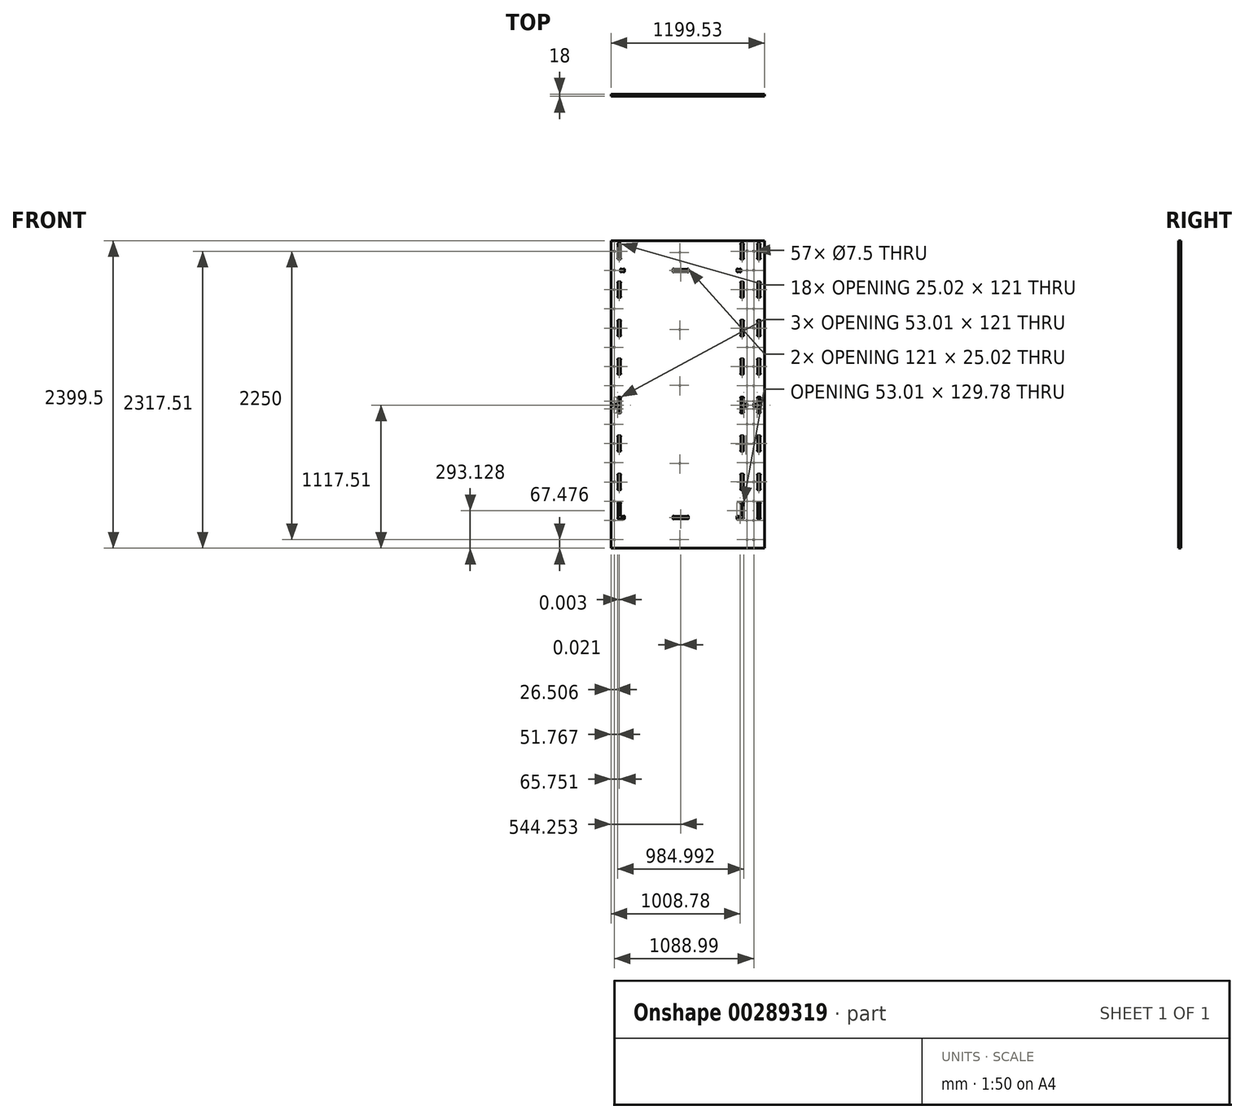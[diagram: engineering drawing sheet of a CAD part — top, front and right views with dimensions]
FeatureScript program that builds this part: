
annotation { "Feature Type Name" : "Feature", "Feature Type Description" : "" }
export const myFeature = defineFeature(function(context is Context, id is Id, definition is map)
    precondition{}
    {
        {
            var Q0;
            Q0=qCreatedBy(makeId("Front.planeOp"),FACE);
            var sketch = newSketch(context, id + "F0", { "sketchPlane" : qUnion([Q0])});
            skLineSegment(sketch, "E0", {"start": v(-600, -1200) * mm, "end": v(600, -1200) * mm});
            skLineSegment(sketch, "E1", {"start": v(600, -1200) * mm, "end": v(600, 1200) * mm});
            skLineSegment(sketch, "E2", {"start": v(600, 1200) * mm, "end": v(-600, 1200) * mm});
            skLineSegment(sketch, "E3", {"start": v(-600, 1200) * mm, "end": v(-600, -1200) * mm});
            skLineSegment(sketch, "E4", {"start": v(599.53, -1200) * mm, "end": v(599.5, 1199.5) * mm});
            skLineSegment(sketch, "E5", {"start": v(599.5, 1199.5) * mm, "end": v(-600, 1199.5) * mm});
            skArc(sketch, "E6", {"start": v(-543.49, 278) * mm, "mid": v(-546.75, 274.87) * mm, "end": v(-543.74, 271.5) * mm});
            skLineSegment(sketch, "E7", {"start": v(-543.74, 271.5) * mm, "end": v(-543.74, 163.52) * mm});
            skArc(sketch, "E8", {"start": v(-543.74, 163.52) * mm, "mid": v(-546.75, 160.14) * mm, "end": v(-543.49, 157) * mm});
            skLineSegment(sketch, "E9", {"start": v(-543.49, 157) * mm, "end": v(-524.99, 157) * mm});
            skArc(sketch, "E10", {"start": v(-524.99, 157) * mm, "mid": v(-521.73, 160.14) * mm, "end": v(-524.74, 163.52) * mm});
            skLineSegment(sketch, "E11", {"start": v(-524.74, 163.52) * mm, "end": v(-524.74, 271.5) * mm});
            skArc(sketch, "E12", {"start": v(-524.74, 271.5) * mm, "mid": v(-521.73, 274.87) * mm, "end": v(-524.99, 278) * mm});
            skLineSegment(sketch, "E13", {"start": v(-524.99, 278) * mm, "end": v(-543.49, 278) * mm});
            skArc(sketch, "E14", {"start": v(-524.74, -28.5) * mm, "mid": v(-521.73, -25.13) * mm, "end": v(-524.99, -22) * mm});
            skLineSegment(sketch, "E15", {"start": v(-524.99, -22) * mm, "end": v(-543.49, -22) * mm});
            skArc(sketch, "E16", {"start": v(-543.49, -22) * mm, "mid": v(-546.75, -25.13) * mm, "end": v(-543.74, -28.5) * mm});
            skLineSegment(sketch, "E17", {"start": v(-543.74, -28.5) * mm, "end": v(-543.74, -73) * mm});
            skLineSegment(sketch, "E18", {"start": v(-543.74, -73) * mm, "end": v(-568.23, -73) * mm});
            skArc(sketch, "E19", {"start": v(-568.23, -73) * mm, "mid": v(-571.6, -69.99) * mm, "end": v(-574.74, -73.25) * mm});
            skLineSegment(sketch, "E20", {"start": v(-574.74, -73.25) * mm, "end": v(-574.74, -91.75) * mm});
            skArc(sketch, "E21", {"start": v(-574.74, -91.75) * mm, "mid": v(-571.6, -95) * mm, "end": v(-568.23, -92) * mm});
            skLineSegment(sketch, "E22", {"start": v(-568.23, -92) * mm, "end": v(-543.74, -92) * mm});
            skLineSegment(sketch, "E23", {"start": v(-543.74, -92) * mm, "end": v(-543.74, -136.48) * mm});
            skArc(sketch, "E24", {"start": v(-543.74, -136.48) * mm, "mid": v(-546.74, -139.86) * mm, "end": v(-543.49, -143) * mm});
            skLineSegment(sketch, "E25", {"start": v(-543.49, -143) * mm, "end": v(-524.99, -143) * mm});
            skArc(sketch, "E26", {"start": v(-524.99, -143) * mm, "mid": v(-521.73, -139.86) * mm, "end": v(-524.74, -136.48) * mm});
            skLineSegment(sketch, "E27", {"start": v(-524.74, -136.48) * mm, "end": v(-524.74, -28.5) * mm});
            skArc(sketch, "E28", {"start": v(-524.73, -328.5) * mm, "mid": v(-521.73, -325.13) * mm, "end": v(-524.98, -322) * mm});
            skLineSegment(sketch, "E29", {"start": v(-524.98, -322) * mm, "end": v(-543.48, -322) * mm});
            skArc(sketch, "E30", {"start": v(-543.48, -322) * mm, "mid": v(-546.74, -325.13) * mm, "end": v(-543.73, -328.5) * mm});
            skLineSegment(sketch, "E31", {"start": v(-543.73, -328.5) * mm, "end": v(-543.73, -436.48) * mm});
            skArc(sketch, "E32", {"start": v(-543.73, -436.48) * mm, "mid": v(-546.74, -439.86) * mm, "end": v(-543.48, -443) * mm});
            skLineSegment(sketch, "E33", {"start": v(-543.48, -443) * mm, "end": v(-524.98, -443) * mm});
            skArc(sketch, "E34", {"start": v(-524.98, -443) * mm, "mid": v(-521.72, -439.86) * mm, "end": v(-524.73, -436.48) * mm});
            skLineSegment(sketch, "E35", {"start": v(-524.73, -436.48) * mm, "end": v(-524.73, -328.5) * mm});
            skArc(sketch, "E36", {"start": v(-524.73, -628.5) * mm, "mid": v(-521.72, -625.13) * mm, "end": v(-524.98, -622) * mm});
            skLineSegment(sketch, "E37", {"start": v(-524.98, -622) * mm, "end": v(-543.48, -622) * mm});
            skArc(sketch, "E38", {"start": v(-543.48, -622) * mm, "mid": v(-546.74, -625.13) * mm, "end": v(-543.73, -628.5) * mm});
            skLineSegment(sketch, "E39", {"start": v(-543.73, -628.5) * mm, "end": v(-543.73, -736.48) * mm});
            skArc(sketch, "E40", {"start": v(-543.73, -736.48) * mm, "mid": v(-546.74, -739.86) * mm, "end": v(-543.48, -743) * mm});
            skLineSegment(sketch, "E41", {"start": v(-543.48, -743) * mm, "end": v(-524.98, -743) * mm});
            skArc(sketch, "E42", {"start": v(-524.98, -743) * mm, "mid": v(-521.72, -739.86) * mm, "end": v(-524.73, -736.48) * mm});
            skLineSegment(sketch, "E43", {"start": v(-524.73, -736.48) * mm, "end": v(-524.73, -628.5) * mm});
            skArc(sketch, "E44", {"start": v(-109.71, -949.76) * mm, "mid": v(-113.1, -946.75) * mm, "end": v(-116.23, -950) * mm});
            skLineSegment(sketch, "E45", {"start": v(-116.23, -950) * mm, "end": v(-116.23, -968.5) * mm});
            skArc(sketch, "E46", {"start": v(-116.23, -968.5) * mm, "mid": v(-113.09, -971.77) * mm, "end": v(-109.71, -968.76) * mm});
            skLineSegment(sketch, "E47", {"start": v(-109.71, -968.76) * mm, "end": v(-1.74, -968.76) * mm});
            skArc(sketch, "E48", {"start": v(-1.74, -968.76) * mm, "mid": v(1.64, -971.76) * mm, "end": v(4.77, -968.5) * mm});
            skLineSegment(sketch, "E49", {"start": v(4.77, -968.5) * mm, "end": v(4.77, -950) * mm});
            skArc(sketch, "E50", {"start": v(4.77, -950) * mm, "mid": v(1.64, -946.75) * mm, "end": v(-1.74, -949.76) * mm});
            skLineSegment(sketch, "E51", {"start": v(-1.74, -949.76) * mm, "end": v(-109.71, -949.76) * mm});
            skArc(sketch, "E52", {"start": v(413.27, -736.47) * mm, "mid": v(410.26, -739.84) * mm, "end": v(413.52, -742.98) * mm});
            skLineSegment(sketch, "E53", {"start": v(413.52, -742.98) * mm, "end": v(432.02, -742.98) * mm});
            skArc(sketch, "E54", {"start": v(432.02, -742.98) * mm, "mid": v(435.28, -739.84) * mm, "end": v(432.27, -736.47) * mm});
            skLineSegment(sketch, "E55", {"start": v(432.27, -736.47) * mm, "end": v(432.27, -628.5) * mm});
            skArc(sketch, "E56", {"start": v(432.27, -628.5) * mm, "mid": v(435.28, -625.11) * mm, "end": v(432.02, -621.98) * mm});
            skLineSegment(sketch, "E57", {"start": v(432.02, -621.98) * mm, "end": v(413.52, -621.98) * mm});
            skArc(sketch, "E58", {"start": v(413.52, -621.98) * mm, "mid": v(410.26, -625.11) * mm, "end": v(413.27, -628.5) * mm});
            skLineSegment(sketch, "E59", {"start": v(413.27, -628.5) * mm, "end": v(413.27, -736.47) * mm});
            skArc(sketch, "E60", {"start": v(432.02, -442.98) * mm, "mid": v(435.28, -439.84) * mm, "end": v(432.27, -436.47) * mm});
            skLineSegment(sketch, "E61", {"start": v(432.27, -436.47) * mm, "end": v(432.27, -328.5) * mm});
            skArc(sketch, "E62", {"start": v(432.27, -328.5) * mm, "mid": v(435.28, -325.11) * mm, "end": v(432.02, -321.98) * mm});
            skLineSegment(sketch, "E63", {"start": v(432.02, -321.98) * mm, "end": v(413.52, -321.98) * mm});
            skArc(sketch, "E64", {"start": v(413.52, -321.98) * mm, "mid": v(410.26, -325.11) * mm, "end": v(413.27, -328.5) * mm});
            skLineSegment(sketch, "E65", {"start": v(413.27, -328.5) * mm, "end": v(413.27, -436.47) * mm});
            skArc(sketch, "E66", {"start": v(413.27, -436.47) * mm, "mid": v(410.26, -439.84) * mm, "end": v(413.52, -442.98) * mm});
            skLineSegment(sketch, "E67", {"start": v(413.52, -442.98) * mm, "end": v(432.02, -442.98) * mm});
            skArc(sketch, "E68", {"start": v(432.01, 157.02) * mm, "mid": v(435.27, 160.16) * mm, "end": v(432.26, 163.53) * mm});
            skLineSegment(sketch, "E69", {"start": v(432.26, 163.53) * mm, "end": v(432.26, 271.51) * mm});
            skArc(sketch, "E70", {"start": v(432.26, 271.51) * mm, "mid": v(435.27, 274.89) * mm, "end": v(432.01, 278.02) * mm});
            skLineSegment(sketch, "E71", {"start": v(432.01, 278.02) * mm, "end": v(413.51, 278.02) * mm});
            skArc(sketch, "E72", {"start": v(413.51, 278.02) * mm, "mid": v(410.25, 274.89) * mm, "end": v(413.26, 271.51) * mm});
            skLineSegment(sketch, "E73", {"start": v(413.26, 271.51) * mm, "end": v(413.26, 163.53) * mm});
            skArc(sketch, "E74", {"start": v(413.26, 163.53) * mm, "mid": v(410.25, 160.16) * mm, "end": v(413.51, 157.02) * mm});
            skLineSegment(sketch, "E75", {"start": v(413.51, 157.02) * mm, "end": v(432.01, 157.02) * mm});
            skArc(sketch, "E76", {"start": v(432, 457.02) * mm, "mid": v(435.27, 460.16) * mm, "end": v(432.26, 463.53) * mm});
            skLineSegment(sketch, "E77", {"start": v(432.26, 463.53) * mm, "end": v(432.26, 571.51) * mm});
            skArc(sketch, "E78", {"start": v(432.26, 571.51) * mm, "mid": v(435.27, 574.89) * mm, "end": v(432, 578.02) * mm});
            skLineSegment(sketch, "E79", {"start": v(432, 578.02) * mm, "end": v(413.5, 578.02) * mm});
            skArc(sketch, "E80", {"start": v(413.5, 578.02) * mm, "mid": v(410.25, 574.89) * mm, "end": v(413.26, 571.51) * mm});
            skLineSegment(sketch, "E81", {"start": v(413.26, 571.51) * mm, "end": v(413.26, 463.53) * mm});
            skArc(sketch, "E82", {"start": v(413.26, 463.53) * mm, "mid": v(410.25, 460.16) * mm, "end": v(413.5, 457.02) * mm});
            skLineSegment(sketch, "E83", {"start": v(413.5, 457.02) * mm, "end": v(432, 457.02) * mm});
            skArc(sketch, "E84", {"start": v(432, 757.02) * mm, "mid": v(435.26, 760.16) * mm, "end": v(432.26, 763.53) * mm});
            skLineSegment(sketch, "E85", {"start": v(432.26, 763.53) * mm, "end": v(432.25, 871.51) * mm});
            skArc(sketch, "E86", {"start": v(432.25, 871.51) * mm, "mid": v(435.26, 874.89) * mm, "end": v(432, 878.02) * mm});
            skLineSegment(sketch, "E87", {"start": v(432, 878.02) * mm, "end": v(413.5, 878.02) * mm});
            skArc(sketch, "E88", {"start": v(413.5, 878.02) * mm, "mid": v(410.25, 874.89) * mm, "end": v(413.25, 871.51) * mm});
            skLineSegment(sketch, "E89", {"start": v(413.25, 871.51) * mm, "end": v(413.26, 763.53) * mm});
            skArc(sketch, "E90", {"start": v(413.26, 763.53) * mm, "mid": v(410.25, 760.16) * mm, "end": v(413.5, 757.02) * mm});
            skLineSegment(sketch, "E91", {"start": v(413.5, 757.02) * mm, "end": v(432, 757.02) * mm});
            skArc(sketch, "E92", {"start": v(545.26, 763.53) * mm, "mid": v(542.25, 760.16) * mm, "end": v(545.5, 757.02) * mm});
            skLineSegment(sketch, "E93", {"start": v(545.5, 757.02) * mm, "end": v(564, 757.02) * mm});
            skArc(sketch, "E94", {"start": v(564, 757.02) * mm, "mid": v(567.26, 760.16) * mm, "end": v(564.26, 763.54) * mm});
            skLineSegment(sketch, "E95", {"start": v(564.26, 763.54) * mm, "end": v(564.25, 871.51) * mm});
            skArc(sketch, "E96", {"start": v(564.25, 871.51) * mm, "mid": v(567.26, 874.89) * mm, "end": v(564, 878.02) * mm});
            skLineSegment(sketch, "E97", {"start": v(564, 878.02) * mm, "end": v(545.5, 878.02) * mm});
            skArc(sketch, "E98", {"start": v(545.5, 878.02) * mm, "mid": v(542.25, 874.89) * mm, "end": v(545.25, 871.51) * mm});
            skLineSegment(sketch, "E99", {"start": v(545.25, 871.51) * mm, "end": v(545.26, 763.53) * mm});
            skArc(sketch, "E100", {"start": v(407.74, 958.01) * mm, "mid": v(411.12, 955) * mm, "end": v(414.25, 958.26) * mm});
            skLineSegment(sketch, "E101", {"start": v(414.25, 958.26) * mm, "end": v(414.25, 976.77) * mm});
            skArc(sketch, "E102", {"start": v(414.25, 976.77) * mm, "mid": v(411.12, 980.03) * mm, "end": v(407.74, 977.02) * mm});
            skLineSegment(sketch, "E103", {"start": v(407.74, 977.02) * mm, "end": v(389.76, 977.02) * mm});
            skArc(sketch, "E104", {"start": v(389.76, 977.02) * mm, "mid": v(386.39, 980.03) * mm, "end": v(383.25, 976.77) * mm});
            skLineSegment(sketch, "E105", {"start": v(383.25, 976.77) * mm, "end": v(383.25, 958.26) * mm});
            skArc(sketch, "E106", {"start": v(383.25, 958.26) * mm, "mid": v(386.39, 955) * mm, "end": v(389.77, 958.01) * mm});
            skLineSegment(sketch, "E107", {"start": v(389.77, 958.01) * mm, "end": v(407.74, 958.01) * mm});
            skArc(sketch, "E108", {"start": v(4.75, 976.76) * mm, "mid": v(1.62, 980.02) * mm, "end": v(-1.76, 977.01) * mm});
            skLineSegment(sketch, "E109", {"start": v(-1.76, 977.01) * mm, "end": v(-109.74, 977.01) * mm});
            skArc(sketch, "E110", {"start": v(-109.74, 977.01) * mm, "mid": v(-113.11, 980.02) * mm, "end": v(-116.25, 976.76) * mm});
            skLineSegment(sketch, "E111", {"start": v(-116.25, 976.76) * mm, "end": v(-116.25, 958.26) * mm});
            skArc(sketch, "E112", {"start": v(-116.25, 958.26) * mm, "mid": v(-113.11, 955) * mm, "end": v(-109.73, 958.01) * mm});
            skLineSegment(sketch, "E113", {"start": v(-109.73, 958.01) * mm, "end": v(-1.76, 958.01) * mm});
            skArc(sketch, "E114", {"start": v(-1.76, 958.01) * mm, "mid": v(1.62, 955) * mm, "end": v(4.75, 958.26) * mm});
            skLineSegment(sketch, "E115", {"start": v(4.75, 958.26) * mm, "end": v(4.75, 976.76) * mm});
            skArc(sketch, "E116", {"start": v(-494.75, 976.76) * mm, "mid": v(-497.88, 980.02) * mm, "end": v(-501.26, 977) * mm});
            skLineSegment(sketch, "E117", {"start": v(-501.26, 977) * mm, "end": v(-519.24, 977) * mm});
            skArc(sketch, "E118", {"start": v(-519.24, 977) * mm, "mid": v(-522.61, 980.02) * mm, "end": v(-525.75, 976.76) * mm});
            skLineSegment(sketch, "E119", {"start": v(-525.75, 976.76) * mm, "end": v(-525.75, 958.26) * mm});
            skArc(sketch, "E120", {"start": v(-525.75, 958.26) * mm, "mid": v(-522.61, 955) * mm, "end": v(-519.24, 958) * mm});
            skLineSegment(sketch, "E121", {"start": v(-519.24, 958) * mm, "end": v(-501.26, 958) * mm});
            skArc(sketch, "E122", {"start": v(-501.26, 958) * mm, "mid": v(-497.88, 955) * mm, "end": v(-494.75, 958.26) * mm});
            skLineSegment(sketch, "E123", {"start": v(-494.75, 958.26) * mm, "end": v(-494.75, 976.76) * mm});
            skArc(sketch, "E124", {"start": v(-543.5, 878) * mm, "mid": v(-546.75, 874.87) * mm, "end": v(-543.75, 871.5) * mm});
            skLineSegment(sketch, "E125", {"start": v(-543.75, 871.5) * mm, "end": v(-543.74, 763.52) * mm});
            skArc(sketch, "E126", {"start": v(-543.74, 763.52) * mm, "mid": v(-546.75, 760.14) * mm, "end": v(-543.5, 757) * mm});
            skLineSegment(sketch, "E127", {"start": v(-543.5, 757) * mm, "end": v(-525, 757) * mm});
            skArc(sketch, "E128", {"start": v(-525, 757) * mm, "mid": v(-521.74, 760.14) * mm, "end": v(-524.75, 763.52) * mm});
            skLineSegment(sketch, "E129", {"start": v(-524.75, 763.52) * mm, "end": v(-524.75, 871.5) * mm});
            skArc(sketch, "E130", {"start": v(-524.75, 871.5) * mm, "mid": v(-521.74, 874.87) * mm, "end": v(-525, 878) * mm});
            skLineSegment(sketch, "E131", {"start": v(-525, 878) * mm, "end": v(-543.5, 878) * mm});
            skArc(sketch, "E132", {"start": v(-524.74, 571.5) * mm, "mid": v(-521.74, 574.87) * mm, "end": v(-525, 578) * mm});
            skLineSegment(sketch, "E133", {"start": v(-525, 578) * mm, "end": v(-543.5, 578) * mm});
            skArc(sketch, "E134", {"start": v(-543.5, 578) * mm, "mid": v(-546.75, 574.87) * mm, "end": v(-543.74, 571.5) * mm});
            skLineSegment(sketch, "E135", {"start": v(-543.74, 571.5) * mm, "end": v(-543.74, 463.52) * mm});
            skArc(sketch, "E136", {"start": v(-543.74, 463.52) * mm, "mid": v(-546.75, 460.14) * mm, "end": v(-543.5, 457) * mm});
            skLineSegment(sketch, "E137", {"start": v(-543.5, 457) * mm, "end": v(-525, 457) * mm});
            skArc(sketch, "E138", {"start": v(-525, 457) * mm, "mid": v(-521.73, 460.14) * mm, "end": v(-524.74, 463.52) * mm});
            skLineSegment(sketch, "E139", {"start": v(-524.74, 463.52) * mm, "end": v(-524.74, 571.5) * mm});
            skArc(sketch, "E140", {"start": v(-525, 1057) * mm, "mid": v(-521.74, 1060.14) * mm, "end": v(-524.75, 1063.52) * mm});
            skLineSegment(sketch, "E141", {"start": v(-524.75, 1063.52) * mm, "end": v(-524.75, 1171.5) * mm});
            skArc(sketch, "E142", {"start": v(-524.75, 1171.5) * mm, "mid": v(-521.74, 1174.87) * mm, "end": v(-525, 1178) * mm});
            skLineSegment(sketch, "E143", {"start": v(-525, 1178) * mm, "end": v(-543.5, 1178) * mm});
            skArc(sketch, "E144", {"start": v(-543.5, 1178) * mm, "mid": v(-546.76, 1174.87) * mm, "end": v(-543.75, 1171.5) * mm});
            skLineSegment(sketch, "E145", {"start": v(-543.75, 1171.5) * mm, "end": v(-543.75, 1063.52) * mm});
            skArc(sketch, "E146", {"start": v(-543.75, 1063.52) * mm, "mid": v(-546.76, 1060.14) * mm, "end": v(-543.5, 1057) * mm});
            skLineSegment(sketch, "E147", {"start": v(-543.5, 1057) * mm, "end": v(-525, 1057) * mm});
            skArc(sketch, "E148", {"start": v(545.25, 1063.54) * mm, "mid": v(542.24, 1060.16) * mm, "end": v(545.5, 1057.02) * mm});
            skLineSegment(sketch, "E149", {"start": v(545.5, 1057.02) * mm, "end": v(564, 1057.02) * mm});
            skArc(sketch, "E150", {"start": v(564, 1057.02) * mm, "mid": v(567.26, 1060.16) * mm, "end": v(564.25, 1063.54) * mm});
            skLineSegment(sketch, "E151", {"start": v(564.25, 1063.54) * mm, "end": v(564.25, 1171.51) * mm});
            skArc(sketch, "E152", {"start": v(564.25, 1171.51) * mm, "mid": v(567.26, 1174.89) * mm, "end": v(564, 1178.02) * mm});
            skLineSegment(sketch, "E153", {"start": v(564, 1178.02) * mm, "end": v(545.5, 1178.02) * mm});
            skArc(sketch, "E154", {"start": v(545.5, 1178.02) * mm, "mid": v(542.24, 1174.89) * mm, "end": v(545.25, 1171.51) * mm});
            skLineSegment(sketch, "E155", {"start": v(545.25, 1171.51) * mm, "end": v(545.25, 1063.54) * mm});
            skLineSegment(sketch, "E156", {"start": v(432.25, 1063.53) * mm, "end": v(432.25, 1171.51) * mm});
            skArc(sketch, "E157", {"start": v(432.25, 1171.51) * mm, "mid": v(435.26, 1174.89) * mm, "end": v(432, 1178.02) * mm});
            skLineSegment(sketch, "E158", {"start": v(432, 1178.02) * mm, "end": v(413.5, 1178.02) * mm});
            skArc(sketch, "E159", {"start": v(413.5, 1178.02) * mm, "mid": v(410.24, 1174.89) * mm, "end": v(413.25, 1171.51) * mm});
            skLineSegment(sketch, "E160", {"start": v(413.25, 1171.51) * mm, "end": v(413.25, 1063.53) * mm});
            skArc(sketch, "E161", {"start": v(413.25, 1063.53) * mm, "mid": v(410.24, 1060.16) * mm, "end": v(413.5, 1057.02) * mm});
            skLineSegment(sketch, "E162", {"start": v(413.5, 1057.02) * mm, "end": v(432, 1057.02) * mm});
            skArc(sketch, "E163", {"start": v(432, 1057.02) * mm, "mid": v(435.26, 1060.16) * mm, "end": v(432.25, 1063.53) * mm});
            skArc(sketch, "E164", {"start": v(545.26, 463.53) * mm, "mid": v(542.25, 460.16) * mm, "end": v(545.5, 457.02) * mm});
            skLineSegment(sketch, "E165", {"start": v(545.5, 457.02) * mm, "end": v(564, 457.02) * mm});
            skArc(sketch, "E166", {"start": v(564, 457.02) * mm, "mid": v(567.27, 460.16) * mm, "end": v(564.26, 463.53) * mm});
            skLineSegment(sketch, "E167", {"start": v(564.26, 463.53) * mm, "end": v(564.26, 571.51) * mm});
            skArc(sketch, "E168", {"start": v(564.26, 571.51) * mm, "mid": v(567.27, 574.89) * mm, "end": v(564, 578.02) * mm});
            skLineSegment(sketch, "E169", {"start": v(564, 578.02) * mm, "end": v(545.5, 578.02) * mm});
            skArc(sketch, "E170", {"start": v(545.5, 578.02) * mm, "mid": v(542.25, 574.89) * mm, "end": v(545.26, 571.51) * mm});
            skLineSegment(sketch, "E171", {"start": v(545.26, 571.51) * mm, "end": v(545.26, 463.53) * mm});
            skArc(sketch, "E172", {"start": v(545.26, 163.53) * mm, "mid": v(542.25, 160.16) * mm, "end": v(545.51, 157.02) * mm});
            skLineSegment(sketch, "E173", {"start": v(545.51, 157.02) * mm, "end": v(564.01, 157.02) * mm});
            skArc(sketch, "E174", {"start": v(564.01, 157.02) * mm, "mid": v(567.27, 160.16) * mm, "end": v(564.26, 163.53) * mm});
            skLineSegment(sketch, "E175", {"start": v(564.26, 163.53) * mm, "end": v(564.26, 271.51) * mm});
            skArc(sketch, "E176", {"start": v(564.26, 271.51) * mm, "mid": v(567.27, 274.89) * mm, "end": v(564.01, 278.02) * mm});
            skLineSegment(sketch, "E177", {"start": v(564.01, 278.02) * mm, "end": v(545.51, 278.02) * mm});
            skArc(sketch, "E178", {"start": v(545.51, 278.02) * mm, "mid": v(542.25, 274.89) * mm, "end": v(545.26, 271.51) * mm});
            skLineSegment(sketch, "E179", {"start": v(545.26, 271.51) * mm, "end": v(545.26, 163.53) * mm});
            skArc(sketch, "E180", {"start": v(545.26, -136.47) * mm, "mid": v(542.26, -139.85) * mm, "end": v(545.51, -142.98) * mm});
            skLineSegment(sketch, "E181", {"start": v(545.51, -142.98) * mm, "end": v(564.01, -142.98) * mm});
            skArc(sketch, "E182", {"start": v(564.01, -142.98) * mm, "mid": v(567.27, -139.85) * mm, "end": v(564.26, -136.47) * mm});
            skLineSegment(sketch, "E183", {"start": v(564.26, -136.47) * mm, "end": v(564.26, -28.5) * mm});
            skArc(sketch, "E184", {"start": v(564.26, -28.5) * mm, "mid": v(567.27, -25.12) * mm, "end": v(564.01, -21.98) * mm});
            skLineSegment(sketch, "E185", {"start": v(564.01, -21.98) * mm, "end": v(545.51, -21.98) * mm});
            skArc(sketch, "E186", {"start": v(545.51, -21.98) * mm, "mid": v(542.25, -25.12) * mm, "end": v(545.26, -28.5) * mm});
            skLineSegment(sketch, "E187", {"start": v(545.26, -28.5) * mm, "end": v(545.26, -72.98) * mm});
            skLineSegment(sketch, "E188", {"start": v(545.26, -72.98) * mm, "end": v(520.77, -72.99) * mm});
            skArc(sketch, "E189", {"start": v(520.77, -72.99) * mm, "mid": v(517.4, -69.98) * mm, "end": v(514.26, -73.24) * mm});
            skLineSegment(sketch, "E190", {"start": v(514.26, -73.24) * mm, "end": v(514.26, -91.74) * mm});
            skArc(sketch, "E191", {"start": v(514.26, -91.74) * mm, "mid": v(517.4, -95) * mm, "end": v(520.77, -91.99) * mm});
            skLineSegment(sketch, "E192", {"start": v(520.77, -91.99) * mm, "end": v(545.26, -91.98) * mm});
            skLineSegment(sketch, "E193", {"start": v(545.26, -91.98) * mm, "end": v(545.26, -136.47) * mm});
            skArc(sketch, "E194", {"start": v(545.27, -436.47) * mm, "mid": v(542.26, -439.84) * mm, "end": v(545.52, -442.98) * mm});
            skLineSegment(sketch, "E195", {"start": v(545.52, -442.98) * mm, "end": v(564.02, -442.98) * mm});
            skArc(sketch, "E196", {"start": v(564.02, -442.98) * mm, "mid": v(567.28, -439.84) * mm, "end": v(564.27, -436.47) * mm});
            skLineSegment(sketch, "E197", {"start": v(564.27, -436.47) * mm, "end": v(564.27, -328.49) * mm});
            skArc(sketch, "E198", {"start": v(564.27, -328.49) * mm, "mid": v(567.28, -325.11) * mm, "end": v(564.02, -321.98) * mm});
            skLineSegment(sketch, "E199", {"start": v(564.02, -321.98) * mm, "end": v(545.52, -321.98) * mm});
            skArc(sketch, "E200", {"start": v(545.52, -321.98) * mm, "mid": v(542.26, -325.11) * mm, "end": v(545.27, -328.49) * mm});
            skLineSegment(sketch, "E201", {"start": v(545.27, -328.49) * mm, "end": v(545.27, -436.47) * mm});
            skArc(sketch, "E202", {"start": v(413.52, -841.98) * mm, "mid": v(410.26, -845.12) * mm, "end": v(413.27, -848.5) * mm});
            skLineSegment(sketch, "E203", {"start": v(413.27, -848.5) * mm, "end": v(413.27, -949.75) * mm});
            skLineSegment(sketch, "E204", {"start": v(413.27, -949.75) * mm, "end": v(388.79, -949.75) * mm});
            skArc(sketch, "E205", {"start": v(388.79, -949.75) * mm, "mid": v(385.4, -946.74) * mm, "end": v(382.27, -950) * mm});
            skLineSegment(sketch, "E206", {"start": v(382.27, -950) * mm, "end": v(382.27, -968.5) * mm});
            skArc(sketch, "E207", {"start": v(382.27, -968.5) * mm, "mid": v(385.41, -971.76) * mm, "end": v(388.79, -968.75) * mm});
            skLineSegment(sketch, "E208", {"start": v(388.79, -968.75) * mm, "end": v(432.02, -968.75) * mm});
            skArc(sketch, "E209", {"start": v(432.02, -968.75) * mm, "mid": v(435.28, -965.62) * mm, "end": v(432.27, -962.24) * mm});
            skLineSegment(sketch, "E210", {"start": v(432.27, -962.24) * mm, "end": v(432.27, -848.5) * mm});
            skArc(sketch, "E211", {"start": v(432.27, -848.5) * mm, "mid": v(435.28, -845.12) * mm, "end": v(432.02, -841.98) * mm});
            skLineSegment(sketch, "E212", {"start": v(432.02, -841.98) * mm, "end": v(413.52, -841.98) * mm});
            skLineSegment(sketch, "E213", {"start": v(545.27, -848.5) * mm, "end": v(545.27, -962.24) * mm});
            skArc(sketch, "E214", {"start": v(545.27, -962.24) * mm, "mid": v(542.27, -965.62) * mm, "end": v(545.52, -968.76) * mm});
            skLineSegment(sketch, "E215", {"start": v(545.52, -968.76) * mm, "end": v(564.02, -968.75) * mm});
            skArc(sketch, "E216", {"start": v(564.02, -968.75) * mm, "mid": v(567.28, -965.62) * mm, "end": v(564.27, -962.24) * mm});
            skLineSegment(sketch, "E217", {"start": v(564.27, -962.24) * mm, "end": v(564.27, -848.5) * mm});
            skArc(sketch, "E218", {"start": v(564.27, -848.5) * mm, "mid": v(567.28, -845.12) * mm, "end": v(564.02, -841.98) * mm});
            skLineSegment(sketch, "E219", {"start": v(564.02, -841.98) * mm, "end": v(545.52, -841.98) * mm});
            skArc(sketch, "E220", {"start": v(545.52, -841.98) * mm, "mid": v(542.26, -845.12) * mm, "end": v(545.27, -848.5) * mm});
            skArc(sketch, "E221", {"start": v(545.27, -736.47) * mm, "mid": v(542.26, -739.84) * mm, "end": v(545.52, -742.98) * mm});
            skLineSegment(sketch, "E222", {"start": v(545.52, -742.98) * mm, "end": v(564.02, -742.98) * mm});
            skArc(sketch, "E223", {"start": v(564.02, -742.98) * mm, "mid": v(567.28, -739.84) * mm, "end": v(564.27, -736.47) * mm});
            skLineSegment(sketch, "E224", {"start": v(564.27, -736.47) * mm, "end": v(564.27, -628.49) * mm});
            skArc(sketch, "E225", {"start": v(564.27, -628.49) * mm, "mid": v(567.28, -625.11) * mm, "end": v(564.02, -621.98) * mm});
            skLineSegment(sketch, "E226", {"start": v(564.02, -621.98) * mm, "end": v(545.52, -621.98) * mm});
            skArc(sketch, "E227", {"start": v(545.52, -621.98) * mm, "mid": v(542.26, -625.11) * mm, "end": v(545.27, -628.49) * mm});
            skLineSegment(sketch, "E228", {"start": v(545.27, -628.49) * mm, "end": v(545.27, -736.47) * mm});
            skArc(sketch, "E229", {"start": v(-543.48, -842) * mm, "mid": v(-546.74, -845.13) * mm, "end": v(-543.73, -848.5) * mm});
            skLineSegment(sketch, "E230", {"start": v(-543.73, -848.5) * mm, "end": v(-543.73, -962.25) * mm});
            skArc(sketch, "E231", {"start": v(-543.73, -962.25) * mm, "mid": v(-546.73, -965.63) * mm, "end": v(-543.48, -968.76) * mm});
            skLineSegment(sketch, "E232", {"start": v(-543.48, -968.76) * mm, "end": v(-500.24, -968.76) * mm});
            skArc(sketch, "E233", {"start": v(-500.24, -968.76) * mm, "mid": v(-496.86, -971.77) * mm, "end": v(-493.73, -968.51) * mm});
            skLineSegment(sketch, "E234", {"start": v(-493.73, -968.51) * mm, "end": v(-493.73, -950.01) * mm});
            skArc(sketch, "E235", {"start": v(-493.73, -950.01) * mm, "mid": v(-496.86, -946.75) * mm, "end": v(-500.24, -949.76) * mm});
            skLineSegment(sketch, "E236", {"start": v(-500.24, -949.76) * mm, "end": v(-524.73, -949.76) * mm});
            skLineSegment(sketch, "E237", {"start": v(-524.73, -949.76) * mm, "end": v(-524.73, -848.5) * mm});
            skArc(sketch, "E238", {"start": v(-524.73, -848.5) * mm, "mid": v(-521.72, -845.13) * mm, "end": v(-524.98, -842) * mm});
            skLineSegment(sketch, "E239", {"start": v(-524.98, -842) * mm, "end": v(-543.48, -842) * mm});
            skArc(sketch, "E240", {"start": v(432.02, -142.98) * mm, "mid": v(435.27, -139.85) * mm, "end": v(432.27, -136.47) * mm});
            skLineSegment(sketch, "E241", {"start": v(432.27, -136.47) * mm, "end": v(432.26, -91.99) * mm});
            skLineSegment(sketch, "E242", {"start": v(432.26, -91.99) * mm, "end": v(456.75, -91.99) * mm});
            skArc(sketch, "E243", {"start": v(456.75, -91.99) * mm, "mid": v(460.13, -95) * mm, "end": v(463.26, -91.74) * mm});
            skLineSegment(sketch, "E244", {"start": v(463.26, -91.74) * mm, "end": v(463.26, -73.24) * mm});
            skArc(sketch, "E245", {"start": v(463.26, -73.24) * mm, "mid": v(460.13, -69.98) * mm, "end": v(456.75, -72.99) * mm});
            skLineSegment(sketch, "E246", {"start": v(456.75, -72.99) * mm, "end": v(432.26, -72.99) * mm});
            skLineSegment(sketch, "E247", {"start": v(432.26, -72.99) * mm, "end": v(432.26, -28.5) * mm});
            skArc(sketch, "E248", {"start": v(432.26, -28.5) * mm, "mid": v(435.27, -25.12) * mm, "end": v(432.01, -21.98) * mm});
            skLineSegment(sketch, "E249", {"start": v(432.01, -21.98) * mm, "end": v(413.51, -21.98) * mm});
            skArc(sketch, "E250", {"start": v(413.51, -21.98) * mm, "mid": v(410.26, -25.12) * mm, "end": v(413.26, -28.5) * mm});
            skLineSegment(sketch, "E251", {"start": v(413.26, -28.5) * mm, "end": v(413.27, -136.47) * mm});
            skArc(sketch, "E252", {"start": v(413.27, -136.47) * mm, "mid": v(410.26, -139.85) * mm, "end": v(413.52, -142.98) * mm});
            skLineSegment(sketch, "E253", {"start": v(413.52, -142.98) * mm, "end": v(432.02, -142.98) * mm});
            skLineSegment(sketch, "E254", {"start": v(-148.8, -55.37) * mm, "end": v(-138.36, -95.37) * mm});
            skLineSegment(sketch, "E255", {"start": v(-138.36, -95.37) * mm, "end": v(-137.25, -95.37) * mm});
            skLineSegment(sketch, "E256", {"start": v(-137.25, -95.37) * mm, "end": v(-126.03, -55.37) * mm});
            skLineSegment(sketch, "E257", {"start": v(-126.03, -55.37) * mm, "end": v(-124.67, -55.37) * mm});
            skLineSegment(sketch, "E258", {"start": v(-124.67, -55.37) * mm, "end": v(-112.71, -95.37) * mm});
            skLineSegment(sketch, "E259", {"start": v(-112.71, -95.37) * mm, "end": v(-111.34, -95.37) * mm});
            skLineSegment(sketch, "E260", {"start": v(-111.34, -95.37) * mm, "end": v(-101.65, -55.37) * mm});
            skLineSegment(sketch, "E261", {"start": v(-102.19, -95.36) * mm, "end": v(-87.88, -55.36) * mm});
            skLineSegment(sketch, "E262", {"start": v(-87.88, -55.36) * mm, "end": v(-85.72, -55.36) * mm});
            skLineSegment(sketch, "E263", {"start": v(-85.72, -55.36) * mm, "end": v(-70.44, -95.36) * mm});
            skLineSegment(sketch, "E264", {"start": v(-97.15, -81.36) * mm, "end": v(-75.9, -81.36) * mm});
            skLineSegment(sketch, "E265", {"start": v(-37.92, -95.35) * mm, "end": v(-61.41, -95.35) * mm});
            skLineSegment(sketch, "E266", {"start": v(-61.41, -95.35) * mm, "end": v(-61.41, -55.4) * mm});
            skLineSegment(sketch, "E267", {"start": v(-5.62, -95.35) * mm, "end": v(-29.12, -95.35) * mm});
            skLineSegment(sketch, "E268", {"start": v(-29.12, -95.35) * mm, "end": v(-29.12, -55.4) * mm});
            skLineSegment(sketch, "E269", {"start": v(31.76, -63.99) * mm, "end": v(31.93, -63.47) * mm});
            skLineSegment(sketch, "E270", {"start": v(31.93, -63.47) * mm, "end": v(32.1, -62.96) * mm});
            skLineSegment(sketch, "E271", {"start": v(32.1, -62.96) * mm, "end": v(32.31, -62.46) * mm});
            skLineSegment(sketch, "E272", {"start": v(32.31, -62.46) * mm, "end": v(32.53, -61.97) * mm});
            skLineSegment(sketch, "E273", {"start": v(32.53, -61.97) * mm, "end": v(32.78, -61.5) * mm});
            skLineSegment(sketch, "E274", {"start": v(32.78, -61.5) * mm, "end": v(33.03, -61.04) * mm});
            skLineSegment(sketch, "E275", {"start": v(33.03, -61.04) * mm, "end": v(33.31, -60.59) * mm});
            skLineSegment(sketch, "E276", {"start": v(33.31, -60.59) * mm, "end": v(33.6, -60.15) * mm});
            skLineSegment(sketch, "E277", {"start": v(33.6, -60.15) * mm, "end": v(33.91, -59.72) * mm});
            skLineSegment(sketch, "E278", {"start": v(33.91, -59.72) * mm, "end": v(34.24, -59.31) * mm});
            skLineSegment(sketch, "E279", {"start": v(34.24, -59.31) * mm, "end": v(34.58, -58.92) * mm});
            skLineSegment(sketch, "E280", {"start": v(34.58, -58.92) * mm, "end": v(34.94, -58.53) * mm});
            skLineSegment(sketch, "E281", {"start": v(34.94, -58.53) * mm, "end": v(35.3, -58.17) * mm});
            skLineSegment(sketch, "E282", {"start": v(35.3, -58.17) * mm, "end": v(35.7, -57.82) * mm});
            skLineSegment(sketch, "E283", {"start": v(35.7, -57.82) * mm, "end": v(36.1, -57.48) * mm});
            skLineSegment(sketch, "E284", {"start": v(36.1, -57.48) * mm, "end": v(36.5, -57.16) * mm});
            skLineSegment(sketch, "E285", {"start": v(36.5, -57.16) * mm, "end": v(36.93, -56.86) * mm});
            skLineSegment(sketch, "E286", {"start": v(36.93, -56.86) * mm, "end": v(37.36, -56.57) * mm});
            skLineSegment(sketch, "E287", {"start": v(37.36, -56.57) * mm, "end": v(37.8, -56.3) * mm});
            skLineSegment(sketch, "E288", {"start": v(37.8, -56.3) * mm, "end": v(38.27, -56.05) * mm});
            skLineSegment(sketch, "E289", {"start": v(38.27, -56.05) * mm, "end": v(38.73, -55.81) * mm});
            skLineSegment(sketch, "E290", {"start": v(38.73, -55.81) * mm, "end": v(39.21, -55.6) * mm});
            skLineSegment(sketch, "E291", {"start": v(39.21, -55.6) * mm, "end": v(39.7, -55.4) * mm});
            skLineSegment(sketch, "E292", {"start": v(39.7, -55.4) * mm, "end": v(40.2, -55.23) * mm});
            skLineSegment(sketch, "E293", {"start": v(40.2, -55.23) * mm, "end": v(40.7, -55.07) * mm});
            skLineSegment(sketch, "E294", {"start": v(40.7, -55.07) * mm, "end": v(41.2, -54.93) * mm});
            skLineSegment(sketch, "E295", {"start": v(41.2, -54.93) * mm, "end": v(41.73, -54.81) * mm});
            skLineSegment(sketch, "E296", {"start": v(41.73, -54.81) * mm, "end": v(42.25, -54.72) * mm});
            skLineSegment(sketch, "E297", {"start": v(42.25, -54.72) * mm, "end": v(42.78, -54.64) * mm});
            skLineSegment(sketch, "E298", {"start": v(42.78, -54.64) * mm, "end": v(43.32, -54.59) * mm});
            skLineSegment(sketch, "E299", {"start": v(43.32, -54.59) * mm, "end": v(43.86, -54.56) * mm});
            skLineSegment(sketch, "E300", {"start": v(43.86, -54.56) * mm, "end": v(44.4, -54.55) * mm});
            skLineSegment(sketch, "E301", {"start": v(44.4, -54.55) * mm, "end": v(45.04, -54.56) * mm});
            skLineSegment(sketch, "E302", {"start": v(45.04, -54.56) * mm, "end": v(45.68, -54.6) * mm});
            skLineSegment(sketch, "E303", {"start": v(45.68, -54.6) * mm, "end": v(46.3, -54.66) * mm});
            skLineSegment(sketch, "E304", {"start": v(46.3, -54.66) * mm, "end": v(46.91, -54.74) * mm});
            skLineSegment(sketch, "E305", {"start": v(46.91, -54.74) * mm, "end": v(47.52, -54.84) * mm});
            skLineSegment(sketch, "E306", {"start": v(47.52, -54.84) * mm, "end": v(48.1, -54.97) * mm});
            skLineSegment(sketch, "E307", {"start": v(48.1, -54.97) * mm, "end": v(48.69, -55.11) * mm});
            skLineSegment(sketch, "E308", {"start": v(48.69, -55.11) * mm, "end": v(49.25, -55.28) * mm});
            skLineSegment(sketch, "E309", {"start": v(49.25, -55.28) * mm, "end": v(49.8, -55.46) * mm});
            skLineSegment(sketch, "E310", {"start": v(49.8, -55.46) * mm, "end": v(50.34, -55.67) * mm});
            skLineSegment(sketch, "E311", {"start": v(50.34, -55.67) * mm, "end": v(50.86, -55.9) * mm});
            skLineSegment(sketch, "E312", {"start": v(50.86, -55.9) * mm, "end": v(51.37, -56.13) * mm});
            skLineSegment(sketch, "E313", {"start": v(51.37, -56.13) * mm, "end": v(51.86, -56.4) * mm});
            skLineSegment(sketch, "E314", {"start": v(51.86, -56.4) * mm, "end": v(52.33, -56.67) * mm});
            skLineSegment(sketch, "E315", {"start": v(52.33, -56.67) * mm, "end": v(52.78, -56.96) * mm});
            skLineSegment(sketch, "E316", {"start": v(52.78, -56.96) * mm, "end": v(53.2, -57.27) * mm});
            skLineSegment(sketch, "E317", {"start": v(53.2, -57.27) * mm, "end": v(53.62, -57.59) * mm});
            skLineSegment(sketch, "E318", {"start": v(53.62, -57.59) * mm, "end": v(54.01, -57.93) * mm});
            skLineSegment(sketch, "E319", {"start": v(54.01, -57.93) * mm, "end": v(54.38, -58.28) * mm});
            skLineSegment(sketch, "E320", {"start": v(54.38, -58.28) * mm, "end": v(54.73, -58.64) * mm});
            skLineSegment(sketch, "E321", {"start": v(54.73, -58.64) * mm, "end": v(55.05, -59.02) * mm});
            skLineSegment(sketch, "E322", {"start": v(55.05, -59.02) * mm, "end": v(55.35, -59.4) * mm});
            skLineSegment(sketch, "E323", {"start": v(55.35, -59.4) * mm, "end": v(55.63, -59.8) * mm});
            skLineSegment(sketch, "E324", {"start": v(55.63, -59.8) * mm, "end": v(55.88, -60.22) * mm});
            skLineSegment(sketch, "E325", {"start": v(55.88, -60.22) * mm, "end": v(56.1, -60.64) * mm});
            skLineSegment(sketch, "E326", {"start": v(56.1, -60.64) * mm, "end": v(56.3, -61.07) * mm});
            skLineSegment(sketch, "E327", {"start": v(56.3, -61.07) * mm, "end": v(56.47, -61.5) * mm});
            skLineSegment(sketch, "E328", {"start": v(56.47, -61.5) * mm, "end": v(56.54, -61.73) * mm});
            skLineSegment(sketch, "E329", {"start": v(56.54, -61.73) * mm, "end": v(56.6, -61.96) * mm});
            skLineSegment(sketch, "E330", {"start": v(56.6, -61.96) * mm, "end": v(56.66, -62.19) * mm});
            skLineSegment(sketch, "E331", {"start": v(56.66, -62.19) * mm, "end": v(56.71, -62.42) * mm});
            skLineSegment(sketch, "E332", {"start": v(56.71, -62.42) * mm, "end": v(56.76, -62.65) * mm});
            skLineSegment(sketch, "E333", {"start": v(56.76, -62.65) * mm, "end": v(56.8, -62.88) * mm});
            skLineSegment(sketch, "E334", {"start": v(56.8, -62.88) * mm, "end": v(56.82, -63.12) * mm});
            skLineSegment(sketch, "E335", {"start": v(56.82, -63.12) * mm, "end": v(56.84, -63.35) * mm});
            skLineSegment(sketch, "E336", {"start": v(56.84, -63.35) * mm, "end": v(56.85, -63.59) * mm});
            skLineSegment(sketch, "E337", {"start": v(56.85, -63.59) * mm, "end": v(56.86, -63.83) * mm});
            skLineSegment(sketch, "E338", {"start": v(56.86, -63.83) * mm, "end": v(56.85, -64.09) * mm});
            skLineSegment(sketch, "E339", {"start": v(56.85, -64.09) * mm, "end": v(56.84, -64.34) * mm});
            skLineSegment(sketch, "E340", {"start": v(56.84, -64.34) * mm, "end": v(56.82, -64.6) * mm});
            skLineSegment(sketch, "E341", {"start": v(56.82, -64.6) * mm, "end": v(56.79, -64.84) * mm});
            skLineSegment(sketch, "E342", {"start": v(56.79, -64.84) * mm, "end": v(56.75, -65.1) * mm});
            skLineSegment(sketch, "E343", {"start": v(56.75, -65.1) * mm, "end": v(56.7, -65.34) * mm});
            skLineSegment(sketch, "E344", {"start": v(56.7, -65.34) * mm, "end": v(56.65, -65.59) * mm});
            skLineSegment(sketch, "E345", {"start": v(56.65, -65.59) * mm, "end": v(56.58, -65.83) * mm});
            skLineSegment(sketch, "E346", {"start": v(56.58, -65.83) * mm, "end": v(56.51, -66.07) * mm});
            skLineSegment(sketch, "E347", {"start": v(56.51, -66.07) * mm, "end": v(56.43, -66.3) * mm});
            skLineSegment(sketch, "E348", {"start": v(56.43, -66.3) * mm, "end": v(56.34, -66.54) * mm});
            skLineSegment(sketch, "E349", {"start": v(56.34, -66.54) * mm, "end": v(56.25, -66.78) * mm});
            skLineSegment(sketch, "E350", {"start": v(56.25, -66.78) * mm, "end": v(56.15, -67.01) * mm});
            skLineSegment(sketch, "E351", {"start": v(56.15, -67.01) * mm, "end": v(56.04, -67.24) * mm});
            skLineSegment(sketch, "E352", {"start": v(56.04, -67.24) * mm, "end": v(55.92, -67.47) * mm});
            skLineSegment(sketch, "E353", {"start": v(55.92, -67.47) * mm, "end": v(55.8, -67.7) * mm});
            skLineSegment(sketch, "E354", {"start": v(55.8, -67.7) * mm, "end": v(55.52, -68.13) * mm});
            skLineSegment(sketch, "E355", {"start": v(55.52, -68.13) * mm, "end": v(55.22, -68.56) * mm});
            skLineSegment(sketch, "E356", {"start": v(55.22, -68.56) * mm, "end": v(54.9, -68.97) * mm});
            skLineSegment(sketch, "E357", {"start": v(54.9, -68.97) * mm, "end": v(54.54, -69.38) * mm});
            skLineSegment(sketch, "E358", {"start": v(54.54, -69.38) * mm, "end": v(54.17, -69.76) * mm});
            skLineSegment(sketch, "E359", {"start": v(54.17, -69.76) * mm, "end": v(53.76, -70.14) * mm});
            skLineSegment(sketch, "E360", {"start": v(53.76, -70.14) * mm, "end": v(53.34, -70.5) * mm});
            skLineSegment(sketch, "E361", {"start": v(53.34, -70.5) * mm, "end": v(52.89, -70.84) * mm});
            skLineSegment(sketch, "E362", {"start": v(52.89, -70.84) * mm, "end": v(52.42, -71.17) * mm});
            skLineSegment(sketch, "E363", {"start": v(52.42, -71.17) * mm, "end": v(51.93, -71.48) * mm});
            skLineSegment(sketch, "E364", {"start": v(51.93, -71.48) * mm, "end": v(51.42, -71.78) * mm});
            skLineSegment(sketch, "E365", {"start": v(51.42, -71.78) * mm, "end": v(50.88, -72.05) * mm});
            skLineSegment(sketch, "E366", {"start": v(50.88, -72.05) * mm, "end": v(50.34, -72.31) * mm});
            skLineSegment(sketch, "E367", {"start": v(50.34, -72.31) * mm, "end": v(49.77, -72.55) * mm});
            skLineSegment(sketch, "E368", {"start": v(49.77, -72.55) * mm, "end": v(49.18, -72.77) * mm});
            skLineSegment(sketch, "E369", {"start": v(49.18, -72.77) * mm, "end": v(48.58, -72.97) * mm});
            skLineSegment(sketch, "E370", {"start": v(48.58, -72.97) * mm, "end": v(47.97, -73.15) * mm});
            skLineSegment(sketch, "E371", {"start": v(47.97, -73.15) * mm, "end": v(47.34, -73.3) * mm});
            skLineSegment(sketch, "E372", {"start": v(47.34, -73.3) * mm, "end": v(46.7, -73.44) * mm});
            skLineSegment(sketch, "E373", {"start": v(46.7, -73.44) * mm, "end": v(46.04, -73.55) * mm});
            skLineSegment(sketch, "E374", {"start": v(46.04, -73.55) * mm, "end": v(45.37, -73.63) * mm});
            skLineSegment(sketch, "E375", {"start": v(45.37, -73.63) * mm, "end": v(44.7, -73.7) * mm});
            skLineSegment(sketch, "E376", {"start": v(44.7, -73.7) * mm, "end": v(44, -73.74) * mm});
            skLineSegment(sketch, "E377", {"start": v(44, -73.74) * mm, "end": v(43.31, -73.75) * mm});
            skLineSegment(sketch, "E378", {"start": v(43.31, -73.75) * mm, "end": v(44.08, -73.76) * mm});
            skLineSegment(sketch, "E379", {"start": v(44.08, -73.76) * mm, "end": v(44.85, -73.8) * mm});
            skLineSegment(sketch, "E380", {"start": v(44.85, -73.8) * mm, "end": v(45.6, -73.87) * mm});
            skLineSegment(sketch, "E381", {"start": v(45.6, -73.87) * mm, "end": v(46.34, -73.96) * mm});
            skLineSegment(sketch, "E382", {"start": v(46.34, -73.96) * mm, "end": v(47.06, -74.08) * mm});
            skLineSegment(sketch, "E383", {"start": v(47.06, -74.08) * mm, "end": v(47.78, -74.22) * mm});
            skLineSegment(sketch, "E384", {"start": v(47.78, -74.22) * mm, "end": v(48.47, -74.39) * mm});
            skLineSegment(sketch, "E385", {"start": v(48.47, -74.39) * mm, "end": v(49.15, -74.58) * mm});
            skLineSegment(sketch, "E386", {"start": v(49.15, -74.58) * mm, "end": v(49.82, -74.8) * mm});
            skLineSegment(sketch, "E387", {"start": v(49.82, -74.8) * mm, "end": v(50.47, -75.02) * mm});
            skLineSegment(sketch, "E388", {"start": v(50.47, -75.02) * mm, "end": v(51.1, -75.28) * mm});
            skLineSegment(sketch, "E389", {"start": v(51.1, -75.28) * mm, "end": v(51.7, -75.55) * mm});
            skLineSegment(sketch, "E390", {"start": v(51.7, -75.55) * mm, "end": v(52.3, -75.85) * mm});
            skLineSegment(sketch, "E391", {"start": v(52.3, -75.85) * mm, "end": v(52.86, -76.16) * mm});
            skLineSegment(sketch, "E392", {"start": v(52.86, -76.16) * mm, "end": v(53.4, -76.5) * mm});
            skLineSegment(sketch, "E393", {"start": v(53.4, -76.5) * mm, "end": v(53.93, -76.84) * mm});
            skLineSegment(sketch, "E394", {"start": v(53.93, -76.84) * mm, "end": v(54.42, -77.2) * mm});
            skLineSegment(sketch, "E395", {"start": v(54.42, -77.2) * mm, "end": v(54.9, -77.6) * mm});
            skLineSegment(sketch, "E396", {"start": v(54.9, -77.6) * mm, "end": v(55.34, -78) * mm});
            skLineSegment(sketch, "E397", {"start": v(55.34, -78) * mm, "end": v(55.76, -78.4) * mm});
            skLineSegment(sketch, "E398", {"start": v(55.76, -78.4) * mm, "end": v(55.96, -78.62) * mm});
            skLineSegment(sketch, "E399", {"start": v(55.96, -78.62) * mm, "end": v(56.15, -78.83) * mm});
            skLineSegment(sketch, "E400", {"start": v(56.15, -78.83) * mm, "end": v(56.33, -79.05) * mm});
            skLineSegment(sketch, "E401", {"start": v(56.33, -79.05) * mm, "end": v(56.51, -79.28) * mm});
            skLineSegment(sketch, "E402", {"start": v(56.51, -79.28) * mm, "end": v(56.68, -79.5) * mm});
            skLineSegment(sketch, "E403", {"start": v(56.68, -79.5) * mm, "end": v(56.84, -79.73) * mm});
            skLineSegment(sketch, "E404", {"start": v(56.84, -79.73) * mm, "end": v(57, -79.96) * mm});
            skLineSegment(sketch, "E405", {"start": v(57, -79.96) * mm, "end": v(57.14, -80.2) * mm});
            skLineSegment(sketch, "E406", {"start": v(57.14, -80.2) * mm, "end": v(57.28, -80.44) * mm});
            skLineSegment(sketch, "E407", {"start": v(57.28, -80.44) * mm, "end": v(57.41, -80.68) * mm});
            skLineSegment(sketch, "E408", {"start": v(57.41, -80.68) * mm, "end": v(57.54, -80.92) * mm});
            skLineSegment(sketch, "E409", {"start": v(57.54, -80.92) * mm, "end": v(57.65, -81.17) * mm});
            skLineSegment(sketch, "E410", {"start": v(57.65, -81.17) * mm, "end": v(57.75, -81.42) * mm});
            skLineSegment(sketch, "E411", {"start": v(57.75, -81.42) * mm, "end": v(57.85, -81.67) * mm});
            skLineSegment(sketch, "E412", {"start": v(57.85, -81.67) * mm, "end": v(57.94, -81.92) * mm});
            skLineSegment(sketch, "E413", {"start": v(57.94, -81.92) * mm, "end": v(58.02, -82.18) * mm});
            skLineSegment(sketch, "E414", {"start": v(58.02, -82.18) * mm, "end": v(58.09, -82.44) * mm});
            skLineSegment(sketch, "E415", {"start": v(58.09, -82.44) * mm, "end": v(58.15, -82.7) * mm});
            skLineSegment(sketch, "E416", {"start": v(58.15, -82.7) * mm, "end": v(58.2, -82.96) * mm});
            skLineSegment(sketch, "E417", {"start": v(58.2, -82.96) * mm, "end": v(58.25, -83.23) * mm});
            skLineSegment(sketch, "E418", {"start": v(58.25, -83.23) * mm, "end": v(58.28, -83.5) * mm});
            skLineSegment(sketch, "E419", {"start": v(58.28, -83.5) * mm, "end": v(58.3, -83.77) * mm});
            skLineSegment(sketch, "E420", {"start": v(58.3, -83.77) * mm, "end": v(58.32, -84.04) * mm});
            skLineSegment(sketch, "E421", {"start": v(58.32, -84.04) * mm, "end": v(58.32, -84.3) * mm});
            skLineSegment(sketch, "E422", {"start": v(58.32, -84.3) * mm, "end": v(58.32, -84.61) * mm});
            skLineSegment(sketch, "E423", {"start": v(58.32, -84.61) * mm, "end": v(58.3, -84.92) * mm});
            skLineSegment(sketch, "E424", {"start": v(58.3, -84.92) * mm, "end": v(58.29, -85.22) * mm});
            skLineSegment(sketch, "E425", {"start": v(58.29, -85.22) * mm, "end": v(58.26, -85.52) * mm});
            skLineSegment(sketch, "E426", {"start": v(58.26, -85.52) * mm, "end": v(58.23, -85.82) * mm});
            skLineSegment(sketch, "E427", {"start": v(58.23, -85.82) * mm, "end": v(58.19, -86.11) * mm});
            skLineSegment(sketch, "E428", {"start": v(58.19, -86.11) * mm, "end": v(58.08, -86.7) * mm});
            skLineSegment(sketch, "E429", {"start": v(58.08, -86.7) * mm, "end": v(57.95, -87.27) * mm});
            skLineSegment(sketch, "E430", {"start": v(57.95, -87.27) * mm, "end": v(57.8, -87.83) * mm});
            skLineSegment(sketch, "E431", {"start": v(57.8, -87.83) * mm, "end": v(57.6, -88.38) * mm});
            skLineSegment(sketch, "E432", {"start": v(57.6, -88.38) * mm, "end": v(57.4, -88.92) * mm});
            skLineSegment(sketch, "E433", {"start": v(57.4, -88.92) * mm, "end": v(57.16, -89.44) * mm});
            skLineSegment(sketch, "E434", {"start": v(57.16, -89.44) * mm, "end": v(56.9, -89.95) * mm});
            skLineSegment(sketch, "E435", {"start": v(56.9, -89.95) * mm, "end": v(56.6, -90.45) * mm});
            skLineSegment(sketch, "E436", {"start": v(56.6, -90.45) * mm, "end": v(56.3, -90.93) * mm});
            skLineSegment(sketch, "E437", {"start": v(56.3, -90.93) * mm, "end": v(55.97, -91.4) * mm});
            skLineSegment(sketch, "E438", {"start": v(55.97, -91.4) * mm, "end": v(55.62, -91.84) * mm});
            skLineSegment(sketch, "E439", {"start": v(55.62, -91.84) * mm, "end": v(55.25, -92.27) * mm});
            skLineSegment(sketch, "E440", {"start": v(55.25, -92.27) * mm, "end": v(54.85, -92.68) * mm});
            skLineSegment(sketch, "E441", {"start": v(54.85, -92.68) * mm, "end": v(54.44, -93.07) * mm});
            skLineSegment(sketch, "E442", {"start": v(54.44, -93.07) * mm, "end": v(54.01, -93.44) * mm});
            skLineSegment(sketch, "E443", {"start": v(54.01, -93.44) * mm, "end": v(53.57, -93.8) * mm});
            skLineSegment(sketch, "E444", {"start": v(53.57, -93.8) * mm, "end": v(53.1, -94.13) * mm});
            skLineSegment(sketch, "E445", {"start": v(53.1, -94.13) * mm, "end": v(52.62, -94.43) * mm});
            skLineSegment(sketch, "E446", {"start": v(52.62, -94.43) * mm, "end": v(52.13, -94.72) * mm});
            skLineSegment(sketch, "E447", {"start": v(52.13, -94.72) * mm, "end": v(51.61, -94.98) * mm});
            skLineSegment(sketch, "E448", {"start": v(51.61, -94.98) * mm, "end": v(51.1, -95.22) * mm});
            skLineSegment(sketch, "E449", {"start": v(51.1, -95.22) * mm, "end": v(50.55, -95.43) * mm});
            skLineSegment(sketch, "E450", {"start": v(50.55, -95.43) * mm, "end": v(50, -95.62) * mm});
            skLineSegment(sketch, "E451", {"start": v(50, -95.62) * mm, "end": v(49.44, -95.78) * mm});
            skLineSegment(sketch, "E452", {"start": v(49.44, -95.78) * mm, "end": v(48.87, -95.9) * mm});
            skLineSegment(sketch, "E453", {"start": v(48.87, -95.9) * mm, "end": v(48.29, -96.01) * mm});
            skLineSegment(sketch, "E454", {"start": v(48.29, -96.01) * mm, "end": v(48, -96.05) * mm});
            skLineSegment(sketch, "E455", {"start": v(48, -96.05) * mm, "end": v(47.7, -96.09) * mm});
            skLineSegment(sketch, "E456", {"start": v(47.7, -96.09) * mm, "end": v(47.4, -96.11) * mm});
            skLineSegment(sketch, "E457", {"start": v(47.4, -96.11) * mm, "end": v(47.1, -96.13) * mm});
            skLineSegment(sketch, "E458", {"start": v(47.1, -96.13) * mm, "end": v(46.79, -96.15) * mm});
            skLineSegment(sketch, "E459", {"start": v(46.79, -96.15) * mm, "end": v(46.48, -96.15) * mm});
            skLineSegment(sketch, "E460", {"start": v(46.48, -96.15) * mm, "end": v(45.04, -96.15) * mm});
            skLineSegment(sketch, "E461", {"start": v(45.04, -96.15) * mm, "end": v(44.38, -96.14) * mm});
            skLineSegment(sketch, "E462", {"start": v(44.38, -96.14) * mm, "end": v(43.73, -96.1) * mm});
            skLineSegment(sketch, "E463", {"start": v(43.73, -96.1) * mm, "end": v(43.08, -96.03) * mm});
            skLineSegment(sketch, "E464", {"start": v(43.08, -96.03) * mm, "end": v(42.44, -95.94) * mm});
            skLineSegment(sketch, "E465", {"start": v(42.44, -95.94) * mm, "end": v(41.8, -95.82) * mm});
            skLineSegment(sketch, "E466", {"start": v(41.8, -95.82) * mm, "end": v(41.17, -95.68) * mm});
            skLineSegment(sketch, "E467", {"start": v(41.17, -95.68) * mm, "end": v(40.55, -95.51) * mm});
            skLineSegment(sketch, "E468", {"start": v(40.55, -95.51) * mm, "end": v(39.94, -95.32) * mm});
            skLineSegment(sketch, "E469", {"start": v(39.94, -95.32) * mm, "end": v(39.34, -95.1) * mm});
            skLineSegment(sketch, "E470", {"start": v(39.34, -95.1) * mm, "end": v(38.74, -94.87) * mm});
            skLineSegment(sketch, "E471", {"start": v(38.74, -94.87) * mm, "end": v(38.16, -94.61) * mm});
            skLineSegment(sketch, "E472", {"start": v(38.16, -94.61) * mm, "end": v(37.6, -94.33) * mm});
            skLineSegment(sketch, "E473", {"start": v(37.6, -94.33) * mm, "end": v(37.03, -94.03) * mm});
            skLineSegment(sketch, "E474", {"start": v(37.03, -94.03) * mm, "end": v(36.49, -93.7) * mm});
            skLineSegment(sketch, "E475", {"start": v(36.49, -93.7) * mm, "end": v(35.95, -93.36) * mm});
            skLineSegment(sketch, "E476", {"start": v(35.95, -93.36) * mm, "end": v(35.43, -93) * mm});
            skLineSegment(sketch, "E477", {"start": v(35.43, -93) * mm, "end": v(34.93, -92.61) * mm});
            skLineSegment(sketch, "E478", {"start": v(34.93, -92.61) * mm, "end": v(34.44, -92.21) * mm});
            skLineSegment(sketch, "E479", {"start": v(34.44, -92.21) * mm, "end": v(33.97, -91.79) * mm});
            skLineSegment(sketch, "E480", {"start": v(33.97, -91.79) * mm, "end": v(33.5, -91.35) * mm});
            skLineSegment(sketch, "E481", {"start": v(33.5, -91.35) * mm, "end": v(33.07, -90.89) * mm});
            skLineSegment(sketch, "E482", {"start": v(33.07, -90.89) * mm, "end": v(32.65, -90.41) * mm});
            skLineSegment(sketch, "E483", {"start": v(32.65, -90.41) * mm, "end": v(32.24, -89.92) * mm});
            skLineSegment(sketch, "E484", {"start": v(32.24, -89.92) * mm, "end": v(31.86, -89.41) * mm});
            skLineSegment(sketch, "E485", {"start": v(31.86, -89.41) * mm, "end": v(31.49, -88.88) * mm});
            skLineSegment(sketch, "E486", {"start": v(31.49, -88.88) * mm, "end": v(31.14, -88.34) * mm});
            skLineSegment(sketch, "E487", {"start": v(31.14, -88.34) * mm, "end": v(30.82, -87.79) * mm});
            skLineSegment(sketch, "E488", {"start": v(30.82, -87.79) * mm, "end": v(30.51, -87.21) * mm});
            skLineSegment(sketch, "E489", {"start": v(30.51, -87.21) * mm, "end": v(30.23, -86.63) * mm});
            skLineSegment(sketch, "E490", {"start": v(30.23, -86.63) * mm, "end": v(29.97, -86.03) * mm});
            skLineSegment(sketch, "E491", {"start": v(29.97, -86.03) * mm, "end": v(29.74, -85.42) * mm});
            skLineSegment(sketch, "E492", {"start": v(29.74, -85.42) * mm, "end": v(29.52, -84.79) * mm});
            skArc(sketch, "E493", {"start": v(519.25, 1117.48) * mm, "mid": v(518.15, 1120.13) * mm, "end": v(515.5, 1121.23) * mm});
            skArc(sketch, "E494", {"start": v(515.5, 1121.23) * mm, "mid": v(512.85, 1120.13) * mm, "end": v(511.75, 1117.48) * mm});
            skArc(sketch, "E495", {"start": v(511.75, 1117.48) * mm, "mid": v(512.85, 1114.82) * mm, "end": v(515.5, 1113.73) * mm});
            skArc(sketch, "E496", {"start": v(515.5, 1113.73) * mm, "mid": v(518.15, 1114.82) * mm, "end": v(519.25, 1117.48) * mm});
            skArc(sketch, "E497", {"start": v(465.74, 1117.48) * mm, "mid": v(464.64, 1120.13) * mm, "end": v(462, 1121.23) * mm});
            skArc(sketch, "E498", {"start": v(462, 1121.23) * mm, "mid": v(459.34, 1120.13) * mm, "end": v(458.24, 1117.48) * mm});
            skArc(sketch, "E499", {"start": v(458.24, 1117.48) * mm, "mid": v(459.34, 1114.82) * mm, "end": v(462, 1113.73) * mm});
            skArc(sketch, "E500", {"start": v(462, 1113.73) * mm, "mid": v(464.64, 1114.82) * mm, "end": v(465.74, 1117.48) * mm});
            skArc(sketch, "E501", {"start": v(519.25, 967.48) * mm, "mid": v(518.15, 970.13) * mm, "end": v(515.5, 971.23) * mm});
            skArc(sketch, "E502", {"start": v(515.5, 971.23) * mm, "mid": v(512.85, 970.13) * mm, "end": v(511.75, 967.48) * mm});
            skArc(sketch, "E503", {"start": v(511.75, 967.48) * mm, "mid": v(512.85, 964.82) * mm, "end": v(515.5, 963.73) * mm});
            skArc(sketch, "E504", {"start": v(515.5, 963.73) * mm, "mid": v(518.15, 964.82) * mm, "end": v(519.25, 967.48) * mm});
            skArc(sketch, "E505", {"start": v(465.74, 967.48) * mm, "mid": v(464.64, 970.13) * mm, "end": v(462, 971.23) * mm});
            skArc(sketch, "E506", {"start": v(462, 971.23) * mm, "mid": v(459.34, 970.13) * mm, "end": v(458.24, 967.48) * mm});
            skArc(sketch, "E507", {"start": v(458.24, 967.48) * mm, "mid": v(459.34, 964.82) * mm, "end": v(462, 963.73) * mm});
            skArc(sketch, "E508", {"start": v(462, 963.73) * mm, "mid": v(464.64, 964.82) * mm, "end": v(465.74, 967.48) * mm});
            skArc(sketch, "E509", {"start": v(519.25, 817.48) * mm, "mid": v(518.15, 820.13) * mm, "end": v(515.5, 821.23) * mm});
            skArc(sketch, "E510", {"start": v(515.5, 821.23) * mm, "mid": v(512.85, 820.13) * mm, "end": v(511.75, 817.48) * mm});
            skArc(sketch, "E511", {"start": v(511.75, 817.48) * mm, "mid": v(512.85, 814.82) * mm, "end": v(515.5, 813.73) * mm});
            skArc(sketch, "E512", {"start": v(515.5, 813.73) * mm, "mid": v(518.15, 814.82) * mm, "end": v(519.25, 817.48) * mm});
            skArc(sketch, "E513", {"start": v(465.74, 817.48) * mm, "mid": v(464.64, 820.13) * mm, "end": v(462, 821.23) * mm});
            skArc(sketch, "E514", {"start": v(462, 821.23) * mm, "mid": v(459.34, 820.13) * mm, "end": v(458.24, 817.48) * mm});
            skArc(sketch, "E515", {"start": v(458.24, 817.48) * mm, "mid": v(459.34, 814.82) * mm, "end": v(462, 813.73) * mm});
            skArc(sketch, "E516", {"start": v(462, 813.73) * mm, "mid": v(464.64, 814.82) * mm, "end": v(465.74, 817.48) * mm});
            skArc(sketch, "E517", {"start": v(519.25, 667.48) * mm, "mid": v(518.15, 670.13) * mm, "end": v(515.5, 671.23) * mm});
            skArc(sketch, "E518", {"start": v(515.5, 671.23) * mm, "mid": v(512.85, 670.13) * mm, "end": v(511.75, 667.48) * mm});
            skArc(sketch, "E519", {"start": v(511.75, 667.48) * mm, "mid": v(512.85, 664.82) * mm, "end": v(515.5, 663.73) * mm});
            skArc(sketch, "E520", {"start": v(515.5, 663.73) * mm, "mid": v(518.15, 664.82) * mm, "end": v(519.25, 667.48) * mm});
            skArc(sketch, "E521", {"start": v(465.74, 667.48) * mm, "mid": v(464.64, 670.13) * mm, "end": v(462, 671.23) * mm});
            skArc(sketch, "E522", {"start": v(462, 671.23) * mm, "mid": v(459.34, 670.13) * mm, "end": v(458.24, 667.48) * mm});
            skArc(sketch, "E523", {"start": v(458.24, 667.48) * mm, "mid": v(459.34, 664.82) * mm, "end": v(462, 663.73) * mm});
            skArc(sketch, "E524", {"start": v(462, 663.73) * mm, "mid": v(464.64, 664.82) * mm, "end": v(465.74, 667.48) * mm});
            skArc(sketch, "E525", {"start": v(519.25, 517.48) * mm, "mid": v(518.15, 520.13) * mm, "end": v(515.5, 521.23) * mm});
            skArc(sketch, "E526", {"start": v(515.5, 521.23) * mm, "mid": v(512.85, 520.13) * mm, "end": v(511.75, 517.48) * mm});
            skArc(sketch, "E527", {"start": v(511.75, 517.48) * mm, "mid": v(512.85, 514.82) * mm, "end": v(515.5, 513.73) * mm});
            skArc(sketch, "E528", {"start": v(515.5, 513.73) * mm, "mid": v(518.15, 514.82) * mm, "end": v(519.25, 517.48) * mm});
            skArc(sketch, "E529", {"start": v(465.74, 517.48) * mm, "mid": v(464.64, 520.13) * mm, "end": v(462, 521.23) * mm});
            skArc(sketch, "E530", {"start": v(462, 521.23) * mm, "mid": v(459.34, 520.13) * mm, "end": v(458.24, 517.48) * mm});
            skArc(sketch, "E531", {"start": v(458.24, 517.48) * mm, "mid": v(459.34, 514.82) * mm, "end": v(462, 513.73) * mm});
            skArc(sketch, "E532", {"start": v(462, 513.73) * mm, "mid": v(464.64, 514.82) * mm, "end": v(465.74, 517.48) * mm});
            skArc(sketch, "E533", {"start": v(519.25, 367.48) * mm, "mid": v(518.15, 370.13) * mm, "end": v(515.5, 371.23) * mm});
            skArc(sketch, "E534", {"start": v(515.5, 371.23) * mm, "mid": v(512.85, 370.13) * mm, "end": v(511.75, 367.48) * mm});
            skArc(sketch, "E535", {"start": v(511.75, 367.48) * mm, "mid": v(512.85, 364.82) * mm, "end": v(515.5, 363.73) * mm});
            skArc(sketch, "E536", {"start": v(515.5, 363.73) * mm, "mid": v(518.15, 364.82) * mm, "end": v(519.25, 367.48) * mm});
            skArc(sketch, "E537", {"start": v(465.74, 367.48) * mm, "mid": v(464.64, 370.13) * mm, "end": v(462, 371.23) * mm});
            skArc(sketch, "E538", {"start": v(462, 371.23) * mm, "mid": v(459.34, 370.13) * mm, "end": v(458.24, 367.48) * mm});
            skArc(sketch, "E539", {"start": v(458.24, 367.48) * mm, "mid": v(459.34, 364.82) * mm, "end": v(462, 363.73) * mm});
            skArc(sketch, "E540", {"start": v(462, 363.73) * mm, "mid": v(464.64, 364.82) * mm, "end": v(465.74, 367.48) * mm});
            skArc(sketch, "E541", {"start": v(519.25, 217.48) * mm, "mid": v(518.15, 220.13) * mm, "end": v(515.5, 221.23) * mm});
            skArc(sketch, "E542", {"start": v(515.5, 221.23) * mm, "mid": v(512.85, 220.13) * mm, "end": v(511.75, 217.48) * mm});
            skArc(sketch, "E543", {"start": v(511.75, 217.48) * mm, "mid": v(512.85, 214.82) * mm, "end": v(515.5, 213.73) * mm});
            skArc(sketch, "E544", {"start": v(515.5, 213.73) * mm, "mid": v(518.15, 214.82) * mm, "end": v(519.25, 217.48) * mm});
            skArc(sketch, "E545", {"start": v(465.74, 217.48) * mm, "mid": v(464.64, 220.13) * mm, "end": v(462, 221.23) * mm});
            skArc(sketch, "E546", {"start": v(462, 221.23) * mm, "mid": v(459.34, 220.13) * mm, "end": v(458.24, 217.48) * mm});
            skArc(sketch, "E547", {"start": v(458.24, 217.48) * mm, "mid": v(459.34, 214.82) * mm, "end": v(462, 213.73) * mm});
            skArc(sketch, "E548", {"start": v(462, 213.73) * mm, "mid": v(464.64, 214.82) * mm, "end": v(465.74, 217.48) * mm});
            skArc(sketch, "E549", {"start": v(519.25, 67.48) * mm, "mid": v(518.15, 70.13) * mm, "end": v(515.5, 71.23) * mm});
            skArc(sketch, "E550", {"start": v(515.5, 71.23) * mm, "mid": v(512.85, 70.13) * mm, "end": v(511.75, 67.48) * mm});
            skArc(sketch, "E551", {"start": v(511.75, 67.48) * mm, "mid": v(512.85, 64.82) * mm, "end": v(515.5, 63.73) * mm});
            skArc(sketch, "E552", {"start": v(515.5, 63.73) * mm, "mid": v(518.15, 64.82) * mm, "end": v(519.25, 67.48) * mm});
            skArc(sketch, "E553", {"start": v(465.74, 67.48) * mm, "mid": v(464.64, 70.13) * mm, "end": v(462, 71.23) * mm});
            skArc(sketch, "E554", {"start": v(462, 71.23) * mm, "mid": v(459.34, 70.13) * mm, "end": v(458.24, 67.48) * mm});
            skArc(sketch, "E555", {"start": v(458.24, 67.48) * mm, "mid": v(459.34, 64.82) * mm, "end": v(462, 63.73) * mm});
            skArc(sketch, "E556", {"start": v(462, 63.73) * mm, "mid": v(464.64, 64.82) * mm, "end": v(465.74, 67.48) * mm});
            skArc(sketch, "E557", {"start": v(519.25, -52.52) * mm, "mid": v(518.15, -49.87) * mm, "end": v(515.5, -48.77) * mm});
            skArc(sketch, "E558", {"start": v(515.5, -48.77) * mm, "mid": v(512.85, -49.87) * mm, "end": v(511.75, -52.52) * mm});
            skArc(sketch, "E559", {"start": v(511.75, -52.52) * mm, "mid": v(512.85, -55.18) * mm, "end": v(515.5, -56.27) * mm});
            skArc(sketch, "E560", {"start": v(515.5, -56.27) * mm, "mid": v(518.15, -55.18) * mm, "end": v(519.25, -52.52) * mm});
            skArc(sketch, "E561", {"start": v(465.74, -52.52) * mm, "mid": v(464.64, -49.87) * mm, "end": v(462, -48.77) * mm});
            skArc(sketch, "E562", {"start": v(462, -48.77) * mm, "mid": v(459.34, -49.87) * mm, "end": v(458.24, -52.52) * mm});
            skArc(sketch, "E563", {"start": v(458.24, -52.52) * mm, "mid": v(459.34, -55.18) * mm, "end": v(462, -56.27) * mm});
            skArc(sketch, "E564", {"start": v(462, -56.27) * mm, "mid": v(464.64, -55.18) * mm, "end": v(465.74, -52.52) * mm});
            skArc(sketch, "E565", {"start": v(519.25, -232.52) * mm, "mid": v(518.15, -229.87) * mm, "end": v(515.5, -228.77) * mm});
            skArc(sketch, "E566", {"start": v(515.5, -228.77) * mm, "mid": v(512.85, -229.87) * mm, "end": v(511.75, -232.52) * mm});
            skArc(sketch, "E567", {"start": v(511.75, -232.52) * mm, "mid": v(512.85, -235.18) * mm, "end": v(515.5, -236.27) * mm});
            skArc(sketch, "E568", {"start": v(515.5, -236.27) * mm, "mid": v(518.15, -235.18) * mm, "end": v(519.25, -232.52) * mm});
            skArc(sketch, "E569", {"start": v(465.74, -232.52) * mm, "mid": v(464.64, -229.87) * mm, "end": v(462, -228.77) * mm});
            skArc(sketch, "E570", {"start": v(462, -228.77) * mm, "mid": v(459.34, -229.87) * mm, "end": v(458.24, -232.52) * mm});
            skArc(sketch, "E571", {"start": v(458.24, -232.52) * mm, "mid": v(459.34, -235.18) * mm, "end": v(462, -236.27) * mm});
            skArc(sketch, "E572", {"start": v(462, -236.27) * mm, "mid": v(464.64, -235.18) * mm, "end": v(465.74, -232.52) * mm});
            skArc(sketch, "E573", {"start": v(519.25, -382.52) * mm, "mid": v(518.15, -379.87) * mm, "end": v(515.5, -378.77) * mm});
            skArc(sketch, "E574", {"start": v(515.5, -378.77) * mm, "mid": v(512.85, -379.87) * mm, "end": v(511.75, -382.52) * mm});
            skArc(sketch, "E575", {"start": v(511.75, -382.52) * mm, "mid": v(512.85, -385.18) * mm, "end": v(515.5, -386.27) * mm});
            skArc(sketch, "E576", {"start": v(515.5, -386.27) * mm, "mid": v(518.15, -385.18) * mm, "end": v(519.25, -382.52) * mm});
            skArc(sketch, "E577", {"start": v(465.74, -382.52) * mm, "mid": v(464.64, -379.87) * mm, "end": v(462, -378.77) * mm});
            skArc(sketch, "E578", {"start": v(462, -378.77) * mm, "mid": v(459.34, -379.87) * mm, "end": v(458.24, -382.52) * mm});
            skArc(sketch, "E579", {"start": v(458.24, -382.52) * mm, "mid": v(459.34, -385.18) * mm, "end": v(462, -386.27) * mm});
            skArc(sketch, "E580", {"start": v(462, -386.27) * mm, "mid": v(464.64, -385.18) * mm, "end": v(465.74, -382.52) * mm});
            skArc(sketch, "E581", {"start": v(519.25, -532.52) * mm, "mid": v(518.15, -529.87) * mm, "end": v(515.5, -528.77) * mm});
            skArc(sketch, "E582", {"start": v(515.5, -528.77) * mm, "mid": v(512.85, -529.87) * mm, "end": v(511.75, -532.52) * mm});
            skArc(sketch, "E583", {"start": v(511.75, -532.52) * mm, "mid": v(512.85, -535.18) * mm, "end": v(515.5, -536.27) * mm});
            skArc(sketch, "E584", {"start": v(515.5, -536.27) * mm, "mid": v(518.15, -535.18) * mm, "end": v(519.25, -532.52) * mm});
            skArc(sketch, "E585", {"start": v(465.74, -532.52) * mm, "mid": v(464.64, -529.87) * mm, "end": v(462, -528.77) * mm});
            skArc(sketch, "E586", {"start": v(462, -528.77) * mm, "mid": v(459.34, -529.87) * mm, "end": v(458.24, -532.52) * mm});
            skArc(sketch, "E587", {"start": v(458.24, -532.52) * mm, "mid": v(459.34, -535.18) * mm, "end": v(462, -536.27) * mm});
            skArc(sketch, "E588", {"start": v(462, -536.27) * mm, "mid": v(464.64, -535.18) * mm, "end": v(465.74, -532.52) * mm});
            skArc(sketch, "E589", {"start": v(519.25, -682.52) * mm, "mid": v(518.15, -679.87) * mm, "end": v(515.5, -678.77) * mm});
            skArc(sketch, "E590", {"start": v(515.5, -678.77) * mm, "mid": v(512.85, -679.87) * mm, "end": v(511.75, -682.52) * mm});
            skArc(sketch, "E591", {"start": v(511.75, -682.52) * mm, "mid": v(512.85, -685.18) * mm, "end": v(515.5, -686.27) * mm});
            skArc(sketch, "E592", {"start": v(515.5, -686.27) * mm, "mid": v(518.15, -685.18) * mm, "end": v(519.25, -682.52) * mm});
            skArc(sketch, "E593", {"start": v(465.74, -682.52) * mm, "mid": v(464.64, -679.87) * mm, "end": v(462, -678.77) * mm});
            skArc(sketch, "E594", {"start": v(462, -678.77) * mm, "mid": v(459.34, -679.87) * mm, "end": v(458.24, -682.52) * mm});
            skArc(sketch, "E595", {"start": v(458.24, -682.52) * mm, "mid": v(459.34, -685.18) * mm, "end": v(462, -686.27) * mm});
            skArc(sketch, "E596", {"start": v(462, -686.27) * mm, "mid": v(464.64, -685.18) * mm, "end": v(465.74, -682.52) * mm});
            skArc(sketch, "E597", {"start": v(519.25, -832.52) * mm, "mid": v(518.15, -829.87) * mm, "end": v(515.5, -828.77) * mm});
            skArc(sketch, "E598", {"start": v(515.5, -828.77) * mm, "mid": v(512.85, -829.87) * mm, "end": v(511.75, -832.52) * mm});
            skArc(sketch, "E599", {"start": v(511.75, -832.52) * mm, "mid": v(512.85, -835.18) * mm, "end": v(515.5, -836.27) * mm});
            skArc(sketch, "E600", {"start": v(515.5, -836.27) * mm, "mid": v(518.15, -835.18) * mm, "end": v(519.25, -832.52) * mm});
            skArc(sketch, "E601", {"start": v(465.74, -832.52) * mm, "mid": v(464.64, -829.87) * mm, "end": v(462, -828.77) * mm});
            skArc(sketch, "E602", {"start": v(462, -828.77) * mm, "mid": v(459.34, -829.87) * mm, "end": v(458.24, -832.52) * mm});
            skArc(sketch, "E603", {"start": v(458.24, -832.52) * mm, "mid": v(459.34, -835.18) * mm, "end": v(462, -836.27) * mm});
            skArc(sketch, "E604", {"start": v(462, -836.27) * mm, "mid": v(464.64, -835.18) * mm, "end": v(465.74, -832.52) * mm});
            skArc(sketch, "E605", {"start": v(519.25, -982.52) * mm, "mid": v(518.15, -979.87) * mm, "end": v(515.5, -978.77) * mm});
            skArc(sketch, "E606", {"start": v(515.5, -978.77) * mm, "mid": v(512.85, -979.87) * mm, "end": v(511.75, -982.52) * mm});
            skArc(sketch, "E607", {"start": v(511.75, -982.52) * mm, "mid": v(512.85, -985.18) * mm, "end": v(515.5, -986.27) * mm});
            skArc(sketch, "E608", {"start": v(515.5, -986.27) * mm, "mid": v(518.15, -985.18) * mm, "end": v(519.25, -982.52) * mm});
            skArc(sketch, "E609", {"start": v(465.74, -982.52) * mm, "mid": v(464.64, -979.87) * mm, "end": v(462, -978.77) * mm});
            skArc(sketch, "E610", {"start": v(462, -978.77) * mm, "mid": v(459.34, -979.87) * mm, "end": v(458.24, -982.52) * mm});
            skArc(sketch, "E611", {"start": v(458.24, -982.52) * mm, "mid": v(459.34, -985.18) * mm, "end": v(462, -986.27) * mm});
            skArc(sketch, "E612", {"start": v(462, -986.27) * mm, "mid": v(464.64, -985.18) * mm, "end": v(465.74, -982.52) * mm});
            skArc(sketch, "E613", {"start": v(519.25, -1132.52) * mm, "mid": v(518.15, -1129.87) * mm, "end": v(515.5, -1128.77) * mm});
            skArc(sketch, "E614", {"start": v(515.5, -1128.77) * mm, "mid": v(512.85, -1129.87) * mm, "end": v(511.75, -1132.52) * mm});
            skArc(sketch, "E615", {"start": v(511.75, -1132.52) * mm, "mid": v(512.85, -1135.18) * mm, "end": v(515.5, -1136.27) * mm});
            skArc(sketch, "E616", {"start": v(515.5, -1136.27) * mm, "mid": v(518.15, -1135.18) * mm, "end": v(519.25, -1132.52) * mm});
            skArc(sketch, "E617", {"start": v(465.74, -1132.52) * mm, "mid": v(464.64, -1129.87) * mm, "end": v(462, -1128.77) * mm});
            skArc(sketch, "E618", {"start": v(462, -1128.77) * mm, "mid": v(459.34, -1129.87) * mm, "end": v(458.24, -1132.52) * mm});
            skArc(sketch, "E619", {"start": v(458.24, -1132.52) * mm, "mid": v(459.34, -1135.18) * mm, "end": v(462, -1136.27) * mm});
            skArc(sketch, "E620", {"start": v(462, -1136.27) * mm, "mid": v(464.64, -1135.18) * mm, "end": v(465.74, -1132.52) * mm});
            skArc(sketch, "E621", {"start": v(519.25, -112.52) * mm, "mid": v(518.15, -109.87) * mm, "end": v(515.5, -108.77) * mm});
            skArc(sketch, "E622", {"start": v(515.5, -108.77) * mm, "mid": v(512.85, -109.87) * mm, "end": v(511.75, -112.52) * mm});
            skArc(sketch, "E623", {"start": v(511.75, -112.52) * mm, "mid": v(512.85, -115.18) * mm, "end": v(515.5, -116.27) * mm});
            skArc(sketch, "E624", {"start": v(515.5, -116.27) * mm, "mid": v(518.15, -115.18) * mm, "end": v(519.25, -112.52) * mm});
            skArc(sketch, "E625", {"start": v(465.74, -112.52) * mm, "mid": v(464.64, -109.87) * mm, "end": v(462, -108.77) * mm});
            skArc(sketch, "E626", {"start": v(462, -108.77) * mm, "mid": v(459.34, -109.87) * mm, "end": v(458.24, -112.52) * mm});
            skArc(sketch, "E627", {"start": v(458.24, -112.52) * mm, "mid": v(459.34, -115.18) * mm, "end": v(462, -116.27) * mm});
            skArc(sketch, "E628", {"start": v(462, -116.27) * mm, "mid": v(464.64, -115.18) * mm, "end": v(465.74, -112.52) * mm});
            skArc(sketch, "E629", {"start": v(-569.74, 1117.48) * mm, "mid": v(-570.84, 1120.13) * mm, "end": v(-573.5, 1121.23) * mm});
            skArc(sketch, "E630", {"start": v(-573.5, 1121.23) * mm, "mid": v(-576.15, 1120.13) * mm, "end": v(-577.24, 1117.48) * mm});
            skArc(sketch, "E631", {"start": v(-577.24, 1117.48) * mm, "mid": v(-576.15, 1114.82) * mm, "end": v(-573.5, 1113.73) * mm});
            skArc(sketch, "E632", {"start": v(-573.5, 1113.73) * mm, "mid": v(-570.84, 1114.82) * mm, "end": v(-569.74, 1117.48) * mm});
            skArc(sketch, "E633", {"start": v(-569.74, 967.48) * mm, "mid": v(-570.84, 970.13) * mm, "end": v(-573.5, 971.23) * mm});
            skArc(sketch, "E634", {"start": v(-573.5, 971.23) * mm, "mid": v(-576.15, 970.13) * mm, "end": v(-577.24, 967.48) * mm});
            skArc(sketch, "E635", {"start": v(-577.24, 967.48) * mm, "mid": v(-576.15, 964.82) * mm, "end": v(-573.5, 963.73) * mm});
            skArc(sketch, "E636", {"start": v(-573.5, 963.73) * mm, "mid": v(-570.84, 964.82) * mm, "end": v(-569.74, 967.48) * mm});
            skArc(sketch, "E637", {"start": v(-569.74, 817.48) * mm, "mid": v(-570.84, 820.13) * mm, "end": v(-573.5, 821.23) * mm});
            skArc(sketch, "E638", {"start": v(-573.5, 821.23) * mm, "mid": v(-576.15, 820.13) * mm, "end": v(-577.24, 817.48) * mm});
            skArc(sketch, "E639", {"start": v(-577.24, 817.48) * mm, "mid": v(-576.15, 814.82) * mm, "end": v(-573.5, 813.73) * mm});
            skArc(sketch, "E640", {"start": v(-573.5, 813.73) * mm, "mid": v(-570.84, 814.82) * mm, "end": v(-569.74, 817.48) * mm});
            skArc(sketch, "E641", {"start": v(-569.74, 667.48) * mm, "mid": v(-570.84, 670.13) * mm, "end": v(-573.5, 671.23) * mm});
            skArc(sketch, "E642", {"start": v(-573.5, 671.23) * mm, "mid": v(-576.15, 670.13) * mm, "end": v(-577.24, 667.48) * mm});
            skArc(sketch, "E643", {"start": v(-577.24, 667.48) * mm, "mid": v(-576.15, 664.82) * mm, "end": v(-573.5, 663.73) * mm});
            skArc(sketch, "E644", {"start": v(-573.5, 663.73) * mm, "mid": v(-570.84, 664.82) * mm, "end": v(-569.74, 667.48) * mm});
            skArc(sketch, "E645", {"start": v(-569.74, 517.48) * mm, "mid": v(-570.84, 520.13) * mm, "end": v(-573.5, 521.23) * mm});
            skArc(sketch, "E646", {"start": v(-573.5, 521.23) * mm, "mid": v(-576.15, 520.13) * mm, "end": v(-577.24, 517.48) * mm});
            skArc(sketch, "E647", {"start": v(-577.24, 517.48) * mm, "mid": v(-576.15, 514.82) * mm, "end": v(-573.5, 513.73) * mm});
            skArc(sketch, "E648", {"start": v(-573.5, 513.73) * mm, "mid": v(-570.84, 514.82) * mm, "end": v(-569.74, 517.48) * mm});
            skArc(sketch, "E649", {"start": v(-569.74, 367.48) * mm, "mid": v(-570.84, 370.13) * mm, "end": v(-573.5, 371.23) * mm});
            skArc(sketch, "E650", {"start": v(-573.5, 371.23) * mm, "mid": v(-576.15, 370.13) * mm, "end": v(-577.24, 367.48) * mm});
            skArc(sketch, "E651", {"start": v(-577.24, 367.48) * mm, "mid": v(-576.15, 364.82) * mm, "end": v(-573.5, 363.73) * mm});
            skArc(sketch, "E652", {"start": v(-573.5, 363.73) * mm, "mid": v(-570.84, 364.82) * mm, "end": v(-569.74, 367.48) * mm});
            skArc(sketch, "E653", {"start": v(-569.74, 217.48) * mm, "mid": v(-570.84, 220.13) * mm, "end": v(-573.5, 221.23) * mm});
            skArc(sketch, "E654", {"start": v(-573.5, 221.23) * mm, "mid": v(-576.15, 220.13) * mm, "end": v(-577.24, 217.48) * mm});
            skArc(sketch, "E655", {"start": v(-577.24, 217.48) * mm, "mid": v(-576.15, 214.82) * mm, "end": v(-573.5, 213.73) * mm});
            skArc(sketch, "E656", {"start": v(-573.5, 213.73) * mm, "mid": v(-570.84, 214.82) * mm, "end": v(-569.74, 217.48) * mm});
            skArc(sketch, "E657", {"start": v(-569.74, 67.48) * mm, "mid": v(-570.84, 70.13) * mm, "end": v(-573.5, 71.23) * mm});
            skArc(sketch, "E658", {"start": v(-573.5, 71.23) * mm, "mid": v(-576.15, 70.13) * mm, "end": v(-577.24, 67.48) * mm});
            skArc(sketch, "E659", {"start": v(-577.24, 67.48) * mm, "mid": v(-576.15, 64.82) * mm, "end": v(-573.5, 63.73) * mm});
            skArc(sketch, "E660", {"start": v(-573.5, 63.73) * mm, "mid": v(-570.84, 64.82) * mm, "end": v(-569.74, 67.48) * mm});
            skArc(sketch, "E661", {"start": v(-569.74, -52.52) * mm, "mid": v(-570.84, -49.87) * mm, "end": v(-573.5, -48.77) * mm});
            skArc(sketch, "E662", {"start": v(-573.5, -48.77) * mm, "mid": v(-576.15, -49.87) * mm, "end": v(-577.24, -52.52) * mm});
            skArc(sketch, "E663", {"start": v(-577.24, -52.52) * mm, "mid": v(-576.15, -55.18) * mm, "end": v(-573.5, -56.27) * mm});
            skArc(sketch, "E664", {"start": v(-573.5, -56.27) * mm, "mid": v(-570.84, -55.18) * mm, "end": v(-569.74, -52.52) * mm});
            skArc(sketch, "E665", {"start": v(-569.74, -232.52) * mm, "mid": v(-570.84, -229.87) * mm, "end": v(-573.5, -228.77) * mm});
            skArc(sketch, "E666", {"start": v(-573.5, -228.77) * mm, "mid": v(-576.15, -229.87) * mm, "end": v(-577.24, -232.52) * mm});
            skArc(sketch, "E667", {"start": v(-577.24, -232.52) * mm, "mid": v(-576.15, -235.18) * mm, "end": v(-573.5, -236.27) * mm});
            skArc(sketch, "E668", {"start": v(-573.5, -236.27) * mm, "mid": v(-570.84, -235.18) * mm, "end": v(-569.74, -232.52) * mm});
            skArc(sketch, "E669", {"start": v(-569.74, -382.52) * mm, "mid": v(-570.84, -379.87) * mm, "end": v(-573.5, -378.77) * mm});
            skArc(sketch, "E670", {"start": v(-573.5, -378.77) * mm, "mid": v(-576.15, -379.87) * mm, "end": v(-577.24, -382.52) * mm});
            skArc(sketch, "E671", {"start": v(-577.24, -382.52) * mm, "mid": v(-576.15, -385.18) * mm, "end": v(-573.5, -386.27) * mm});
            skArc(sketch, "E672", {"start": v(-573.5, -386.27) * mm, "mid": v(-570.84, -385.18) * mm, "end": v(-569.74, -382.52) * mm});
            skArc(sketch, "E673", {"start": v(-569.74, -532.52) * mm, "mid": v(-570.84, -529.87) * mm, "end": v(-573.5, -528.77) * mm});
            skArc(sketch, "E674", {"start": v(-573.5, -528.77) * mm, "mid": v(-576.15, -529.87) * mm, "end": v(-577.24, -532.52) * mm});
            skArc(sketch, "E675", {"start": v(-577.24, -532.52) * mm, "mid": v(-576.15, -535.18) * mm, "end": v(-573.5, -536.27) * mm});
            skArc(sketch, "E676", {"start": v(-573.5, -536.27) * mm, "mid": v(-570.84, -535.18) * mm, "end": v(-569.74, -532.52) * mm});
            skArc(sketch, "E677", {"start": v(-569.74, -682.52) * mm, "mid": v(-570.84, -679.87) * mm, "end": v(-573.5, -678.77) * mm});
            skArc(sketch, "E678", {"start": v(-573.5, -678.77) * mm, "mid": v(-576.15, -679.87) * mm, "end": v(-577.24, -682.52) * mm});
            skArc(sketch, "E679", {"start": v(-577.24, -682.52) * mm, "mid": v(-576.15, -685.18) * mm, "end": v(-573.5, -686.27) * mm});
            skArc(sketch, "E680", {"start": v(-573.5, -686.27) * mm, "mid": v(-570.84, -685.18) * mm, "end": v(-569.74, -682.52) * mm});
            skArc(sketch, "E681", {"start": v(-569.74, -832.52) * mm, "mid": v(-570.84, -829.87) * mm, "end": v(-573.5, -828.77) * mm});
            skArc(sketch, "E682", {"start": v(-573.5, -828.77) * mm, "mid": v(-576.15, -829.87) * mm, "end": v(-577.24, -832.52) * mm});
            skArc(sketch, "E683", {"start": v(-577.24, -832.52) * mm, "mid": v(-576.15, -835.18) * mm, "end": v(-573.5, -836.27) * mm});
            skArc(sketch, "E684", {"start": v(-573.5, -836.27) * mm, "mid": v(-570.84, -835.18) * mm, "end": v(-569.74, -832.52) * mm});
            skArc(sketch, "E685", {"start": v(-569.74, -982.52) * mm, "mid": v(-570.84, -979.87) * mm, "end": v(-573.5, -978.77) * mm});
            skArc(sketch, "E686", {"start": v(-573.5, -978.77) * mm, "mid": v(-576.15, -979.87) * mm, "end": v(-577.24, -982.52) * mm});
            skArc(sketch, "E687", {"start": v(-577.24, -982.52) * mm, "mid": v(-576.15, -985.18) * mm, "end": v(-573.5, -986.27) * mm});
            skArc(sketch, "E688", {"start": v(-573.5, -986.27) * mm, "mid": v(-570.84, -985.18) * mm, "end": v(-569.74, -982.52) * mm});
            skArc(sketch, "E689", {"start": v(-569.74, -1132.52) * mm, "mid": v(-570.84, -1129.87) * mm, "end": v(-573.5, -1128.77) * mm});
            skArc(sketch, "E690", {"start": v(-573.5, -1128.77) * mm, "mid": v(-576.15, -1129.87) * mm, "end": v(-577.24, -1132.52) * mm});
            skArc(sketch, "E691", {"start": v(-577.24, -1132.52) * mm, "mid": v(-576.15, -1135.18) * mm, "end": v(-573.5, -1136.27) * mm});
            skArc(sketch, "E692", {"start": v(-573.5, -1136.27) * mm, "mid": v(-570.84, -1135.18) * mm, "end": v(-569.74, -1132.52) * mm});
            skArc(sketch, "E693", {"start": v(-569.74, -112.52) * mm, "mid": v(-570.84, -109.87) * mm, "end": v(-573.5, -108.77) * mm});
            skArc(sketch, "E694", {"start": v(-573.5, -108.77) * mm, "mid": v(-576.15, -109.87) * mm, "end": v(-577.24, -112.52) * mm});
            skArc(sketch, "E695", {"start": v(-577.24, -112.52) * mm, "mid": v(-576.15, -115.18) * mm, "end": v(-573.5, -116.27) * mm});
            skArc(sketch, "E696", {"start": v(-573.5, -116.27) * mm, "mid": v(-570.84, -115.18) * mm, "end": v(-569.74, -112.52) * mm});
            skArc(sketch, "E697", {"start": v(-61.9, 1111.02) * mm, "mid": v(-64.55, 1109.92) * mm, "end": v(-65.64, 1107.27) * mm});
            skArc(sketch, "E698", {"start": v(-65.64, 1107.27) * mm, "mid": v(-64.55, 1104.62) * mm, "end": v(-61.9, 1103.52) * mm});
            skArc(sketch, "E699", {"start": v(-61.9, 1103.52) * mm, "mid": v(-59.24, 1104.62) * mm, "end": v(-58.14, 1107.27) * mm});
            skArc(sketch, "E700", {"start": v(-58.14, 1107.27) * mm, "mid": v(-59.24, 1109.92) * mm, "end": v(-61.9, 1111.02) * mm});
            skArc(sketch, "E701", {"start": v(-61.9, 510.14) * mm, "mid": v(-64.55, 509.04) * mm, "end": v(-65.64, 506.4) * mm});
            skArc(sketch, "E702", {"start": v(-65.64, 506.4) * mm, "mid": v(-64.55, 503.74) * mm, "end": v(-61.9, 502.64) * mm});
            skArc(sketch, "E703", {"start": v(-61.9, 502.64) * mm, "mid": v(-59.24, 503.74) * mm, "end": v(-58.14, 506.4) * mm});
            skArc(sketch, "E704", {"start": v(-58.14, 506.4) * mm, "mid": v(-59.24, 509.04) * mm, "end": v(-61.9, 510.14) * mm});
            skArc(sketch, "E705", {"start": v(-61.9, 74.5) * mm, "mid": v(-64.55, 73.4) * mm, "end": v(-65.64, 70.75) * mm});
            skArc(sketch, "E706", {"start": v(-65.64, 70.75) * mm, "mid": v(-64.55, 68.1) * mm, "end": v(-61.9, 67) * mm});
            skArc(sketch, "E707", {"start": v(-61.9, 67) * mm, "mid": v(-59.24, 68.1) * mm, "end": v(-58.14, 70.75) * mm});
            skArc(sketch, "E708", {"start": v(-58.14, 70.75) * mm, "mid": v(-59.24, 73.4) * mm, "end": v(-61.9, 74.5) * mm});
            skArc(sketch, "E709", {"start": v(-61.9, -534.06) * mm, "mid": v(-64.55, -535.16) * mm, "end": v(-65.64, -537.81) * mm});
            skArc(sketch, "E710", {"start": v(-65.64, -537.81) * mm, "mid": v(-64.55, -540.47) * mm, "end": v(-61.9, -541.56) * mm});
            skArc(sketch, "E711", {"start": v(-61.9, -541.56) * mm, "mid": v(-59.24, -540.47) * mm, "end": v(-58.14, -537.81) * mm});
            skArc(sketch, "E712", {"start": v(-58.14, -537.81) * mm, "mid": v(-59.24, -535.16) * mm, "end": v(-61.9, -534.06) * mm});
            skArc(sketch, "E713", {"start": v(-61.9, -1127.22) * mm, "mid": v(-64.55, -1128.32) * mm, "end": v(-65.64, -1130.97) * mm});
            skArc(sketch, "E714", {"start": v(-65.64, -1130.97) * mm, "mid": v(-64.55, -1133.62) * mm, "end": v(-61.9, -1134.72) * mm});
            skArc(sketch, "E715", {"start": v(-61.9, -1134.72) * mm, "mid": v(-59.24, -1133.62) * mm, "end": v(-58.14, -1130.97) * mm});
            skArc(sketch, "E716", {"start": v(-58.14, -1130.97) * mm, "mid": v(-59.24, -1128.32) * mm, "end": v(-61.9, -1127.22) * mm});
            skArc(sketch, "E717", {"start": v(451.73, -384.8) * mm, "mid": v(449.08, -385.9) * mm, "end": v(447.98, -388.55) * mm});
            skArc(sketch, "E718", {"start": v(447.98, -388.55) * mm, "mid": v(449.08, -391.2) * mm, "end": v(451.73, -392.3) * mm});
            skArc(sketch, "E719", {"start": v(451.73, -392.3) * mm, "mid": v(454.39, -391.2) * mm, "end": v(455.48, -388.55) * mm});
            skArc(sketch, "E720", {"start": v(455.48, -388.55) * mm, "mid": v(454.39, -385.9) * mm, "end": v(451.73, -384.8) * mm});
            skSolve(sketch);
        }
        {
            var Q0;
            {var subQ1=sQuery(id+"F0.wireOp",EDGE,"E4");Q0=makeQuery(id+"F0.imprint","IMPRINT",FACE,{"disambiguationData":[TD([[makeQuery(id+"F0.imprint","IMPRINT",EDGE,{"derivedFrom":subQ1}),1.0]])]});}
            extrude(context, id + "F1", {"entities" : qUnion([Q0]), "depth" : 18 * mm});
        }
    });
